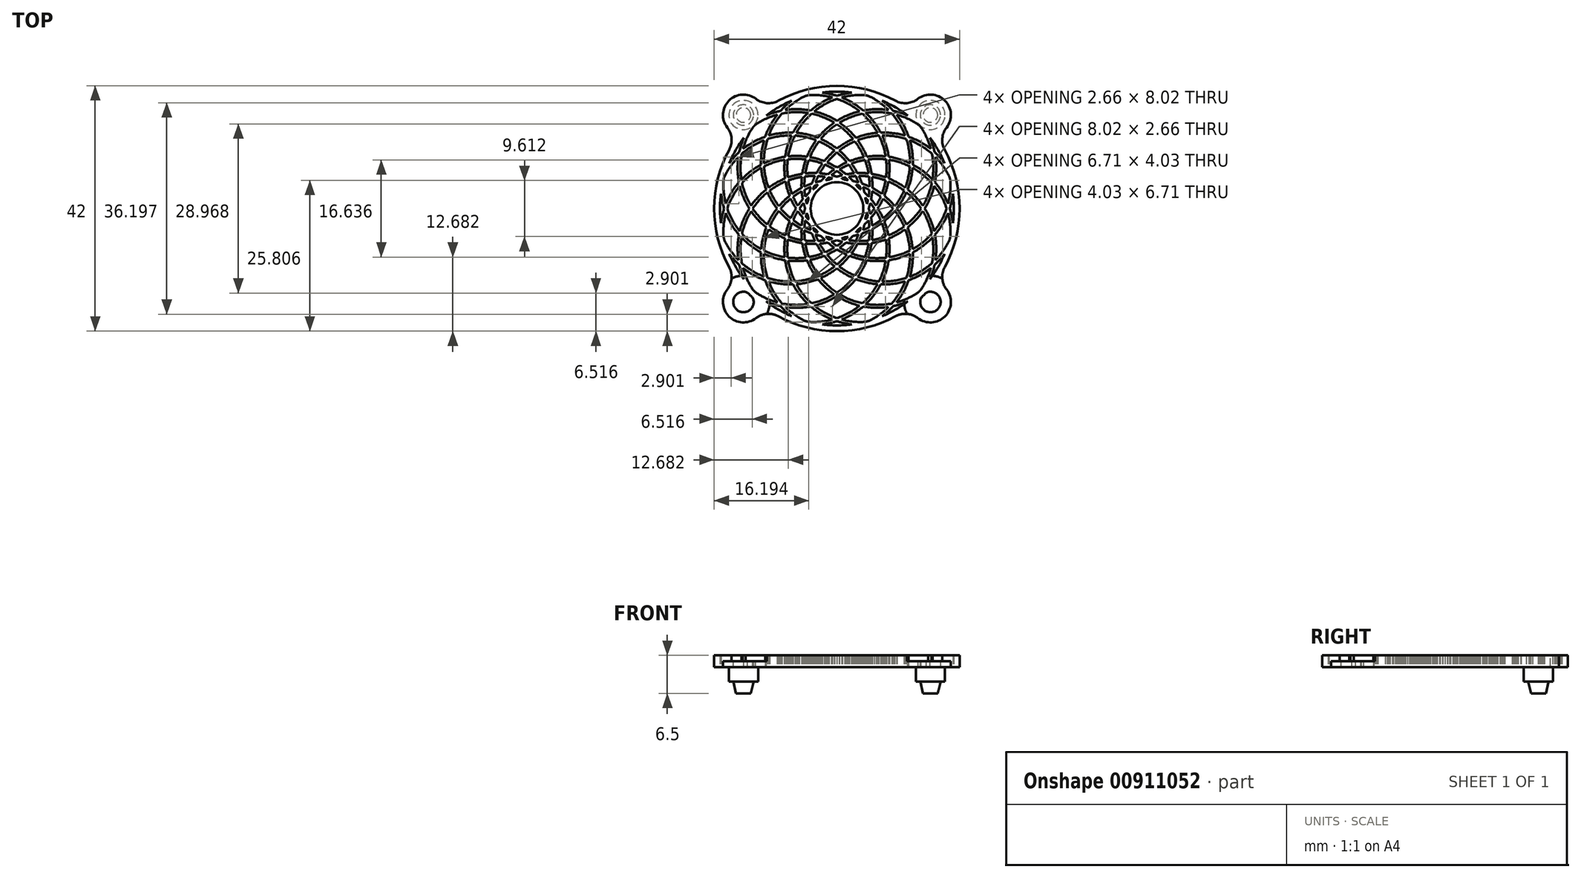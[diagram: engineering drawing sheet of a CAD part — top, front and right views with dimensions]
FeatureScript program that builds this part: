
annotation { "Feature Type Name" : "Feature", "Feature Type Description" : "" }
export const myFeature = defineFeature(function(context is Context, id is Id, definition is map)
    precondition{}
    {
        {
            var Q0;
            Q0=qCreatedBy(makeId("Top.planeOp"),FACE);
            var sketch = newSketch(context, id + "F0", { "sketchPlane" : qUnion([Q0])});
            skArc(sketch, "E0", {"start": v(-16.8, 12.6) * mm, "mid": v(-21, 0) * mm, "end": v(-16.8, -12.6) * mm});
            skArc(sketch, "E1", {"start": v(-7.75, 18.44) * mm, "mid": v(-8.74, 17.62) * mm, "end": v(-9.65, 16.71) * mm});
            skArc(sketch, "E2.1.0", {"start": v(-15.93, 12.1) * mm, "mid": v(-16.38, 10.89) * mm, "end": v(-16.71, 9.65) * mm});
            skArc(sketch, "E2.2.0", {"start": v(-19.84, 2.5) * mm, "mid": v(-19.63, 1.24) * mm, "end": v(-19.3, 0) * mm});
            skArc(sketch, "E2.3.0", {"start": v(-18.44, -7.75) * mm, "mid": v(-17.62, -8.74) * mm, "end": v(-16.71, -9.65) * mm});
            skArc(sketch, "E2.4.0", {"start": v(-19.3, 0) * mm, "mid": v(-19.63, -1.24) * mm, "end": v(-19.84, -2.5) * mm});
            skArc(sketch, "E2.5.0", {"start": v(-2.5, -19.84) * mm, "mid": v(-1.24, -19.63) * mm, "end": v(0, -19.3) * mm});
            skArc(sketch, "E2.6.0", {"start": v(7.75, -18.44) * mm, "mid": v(8.74, -17.62) * mm, "end": v(9.65, -16.71) * mm});
            skArc(sketch, "E2.7.0", {"start": v(15.93, -12.1) * mm, "mid": v(16.38, -10.89) * mm, "end": v(16.71, -9.65) * mm});
            skArc(sketch, "E2.8.0", {"start": v(19.84, -2.5) * mm, "mid": v(19.63, -1.24) * mm, "end": v(19.3, 0) * mm});
            skArc(sketch, "E2.9.0", {"start": v(18.44, 7.75) * mm, "mid": v(17.62, 8.74) * mm, "end": v(16.71, 9.65) * mm});
            skArc(sketch, "E2.10.0", {"start": v(12.1, 15.93) * mm, "mid": v(10.89, 16.38) * mm, "end": v(9.65, 16.71) * mm});
            skArc(sketch, "E2.11.0", {"start": v(2.5, 19.84) * mm, "mid": v(1.24, 19.63) * mm, "end": v(0, 19.3) * mm});
            skArc(sketch, "E3", {"start": v(16.8, 12.6) * mm, "mid": v(18.47, 18.47) * mm, "end": v(12.6, 16.8) * mm});
            skArc(sketch, "E4.3.0", {"start": v(12.6, -16.8) * mm, "mid": v(18.47, -18.47) * mm, "end": v(16.8, -12.6) * mm});
            skArc(sketch, "E5.2.0", {"start": v(-15.28, -14.4) * mm, "mid": v(-17.24, -17.24) * mm, "end": v(-14.4, -15.28) * mm});
            skArc(sketch, "E6.1.3.0", {"start": v(14.4, -15.28) * mm, "mid": v(17.24, -17.24) * mm, "end": v(15.28, -14.4) * mm});
            skPoint(sketch, "E7.orphan", {"position": v(-16, 16) * mm});
            skArc(sketch, "E8.trimOffspring", {"start": v(-12.6, 16.8) * mm, "mid": v(-18.47, 18.47) * mm, "end": v(-16.8, 12.6) * mm});
            skArc(sketch, "E9.trimOffspring", {"start": v(-16.8, -12.6) * mm, "mid": v(-18.47, -18.47) * mm, "end": v(-12.6, -16.8) * mm});
            skArc(sketch, "E10", {"start": v(14.36, 13.92) * mm, "mid": v(14.14, 14.14) * mm, "end": v(13.92, 14.36) * mm});
            skArc(sketch, "E11", {"start": v(-5.48, 19.23) * mm, "mid": v(-7.25, 18.19) * mm, "end": v(-8.82, 16.86) * mm});
            skArc(sketch, "E12.1.0", {"start": v(-14.36, 13.92) * mm, "mid": v(-15.37, 12.13) * mm, "end": v(-16.07, 10.2) * mm});
            skArc(sketch, "E12.2.0", {"start": v(-19.37, 5.2) * mm, "mid": v(-19.39, 2.98) * mm, "end": v(-19.01, 0.8) * mm});
            skArc(sketch, "E12.3.0", {"start": v(-16.86, 8.82) * mm, "mid": v(-18.28, 7.11) * mm, "end": v(-19.37, 5.2) * mm});
            skArc(sketch, "E12.4.0", {"start": v(-19.01, -0.8) * mm, "mid": v(-19.37, -2.82) * mm, "end": v(-19.4, -4.87) * mm});
            skArc(sketch, "E12.5.0", {"start": v(-4.87, -19.4) * mm, "mid": v(-2.82, -19.37) * mm, "end": v(-0.8, -19.01) * mm});
            skArc(sketch, "E12.6.0", {"start": v(5.48, -19.23) * mm, "mid": v(7.25, -18.19) * mm, "end": v(8.82, -16.86) * mm});
            skArc(sketch, "E12.7.0", {"start": v(14.36, -13.92) * mm, "mid": v(15.37, -12.13) * mm, "end": v(16.07, -10.2) * mm});
            skArc(sketch, "E12.8.0", {"start": v(19.4, -4.87) * mm, "mid": v(19.37, -2.82) * mm, "end": v(19.01, -0.8) * mm});
            skArc(sketch, "E12.9.0", {"start": v(19.23, 5.48) * mm, "mid": v(18.19, 7.25) * mm, "end": v(16.86, 8.82) * mm});
            skArc(sketch, "E12.10.0", {"start": v(13.92, 14.36) * mm, "mid": v(12.13, 15.37) * mm, "end": v(10.2, 16.07) * mm});
            skArc(sketch, "E12.11.0", {"start": v(4.87, 19.4) * mm, "mid": v(2.82, 19.37) * mm, "end": v(0.8, 19.01) * mm});
            skCircle(sketch, "E13", {"center": v(0, 0) * mm, "radius": 4.5 * mm});
            skArc(sketch, "E14.trimOffspring", {"start": v(12.6, 16.8) * mm, "mid": v(0, 21) * mm, "end": v(-12.6, 16.8) * mm});
            skArc(sketch, "E15.trimOffspring", {"start": v(12.1, 15.93) * mm, "mid": v(10, 17.32) * mm, "end": v(7.75, 18.44) * mm});
            skArc(sketch, "E16.trimOffspring", {"start": v(-7.75, 18.44) * mm, "mid": v(-10, 17.32) * mm, "end": v(-12.1, 15.93) * mm});
            skArc(sketch, "E17.trimOffspring", {"start": v(-4.87, 19.4) * mm, "mid": v(-5.18, 19.32) * mm, "end": v(-5.48, 19.23) * mm});
            skArc(sketch, "E18.trimOffspring", {"start": v(-13.92, 14.36) * mm, "mid": v(-14.14, 14.14) * mm, "end": v(-14.36, 13.92) * mm});
            skArc(sketch, "E19.trimOffspring", {"start": v(-15.93, 12.1) * mm, "mid": v(-17.32, 10) * mm, "end": v(-18.44, 7.75) * mm});
            skArc(sketch, "E20.trimOffspring", {"start": v(-16.86, 8.82) * mm, "mid": v(-17, 6.65) * mm, "end": v(-16.77, 4.5) * mm});
            skArc(sketch, "E21.trimOffspring", {"start": v(-16.71, 9.65) * mm, "mid": v(-17.62, 8.74) * mm, "end": v(-18.44, 7.75) * mm});
            skArc(sketch, "E22.trimOffspring", {"start": v(-16.26, 9.39) * mm, "mid": v(-16.31, 4.78) * mm, "end": v(-14.7, 0.46) * mm});
            skArc(sketch, "E23.trimOffspring", {"start": v(-19.23, -5.48) * mm, "mid": v(-18.19, -7.25) * mm, "end": v(-16.86, -8.82) * mm});
            skArc(sketch, "E24.trimOffspring", {"start": v(-19.84, 2.5) * mm, "mid": v(-20, 0) * mm, "end": v(-19.84, -2.5) * mm});
            skArc(sketch, "E25.trimOffspring", {"start": v(-18.77, 0) * mm, "mid": v(-17.88, -2.03) * mm, "end": v(-16.64, -3.87) * mm});
            skArc(sketch, "E26.trimOffspring", {"start": v(-19.01, -0.8) * mm, "mid": v(-18.05, -2.74) * mm, "end": v(-16.77, -4.5) * mm});
            skArc(sketch, "E27.trimOffspring", {"start": v(-19.4, -4.87) * mm, "mid": v(-19.32, -5.18) * mm, "end": v(-19.23, -5.48) * mm});
            skArc(sketch, "E28.trimOffspring", {"start": v(-18.44, -7.75) * mm, "mid": v(-17.32, -10) * mm, "end": v(-15.93, -12.1) * mm});
            skArc(sketch, "E29.trimOffspring", {"start": v(-13.92, -14.36) * mm, "mid": v(-12.13, -15.37) * mm, "end": v(-10.2, -16.07) * mm});
            skArc(sketch, "E30.trimOffspring", {"start": v(19.4, 4.87) * mm, "mid": v(19.32, 5.18) * mm, "end": v(19.23, 5.48) * mm});
            skArc(sketch, "E31.trimOffspring", {"start": v(18.44, 7.75) * mm, "mid": v(17.32, 10) * mm, "end": v(15.93, 12.1) * mm});
            skArc(sketch, "E32.trimOffspring", {"start": v(5.48, 19.23) * mm, "mid": v(5.18, 19.32) * mm, "end": v(4.87, 19.4) * mm});
            skArc(sketch, "E33.trimOffspring", {"start": v(2.5, 19.84) * mm, "mid": v(0, 20) * mm, "end": v(-2.5, 19.84) * mm});
            skArc(sketch, "E34.trimOffspring", {"start": v(15.93, -12.1) * mm, "mid": v(17.32, -10) * mm, "end": v(18.44, -7.75) * mm});
            skArc(sketch, "E35.trimOffspring", {"start": v(19.23, -5.48) * mm, "mid": v(19.32, -5.18) * mm, "end": v(19.4, -4.87) * mm});
            skArc(sketch, "E36.trimOffspring", {"start": v(14.4, -15.28) * mm, "mid": v(14.85, -14.85) * mm, "end": v(15.28, -14.4) * mm});
            skArc(sketch, "E37.trimOffspring", {"start": v(13.92, -14.36) * mm, "mid": v(14.14, -14.14) * mm, "end": v(14.36, -13.92) * mm});
            skArc(sketch, "E38.trimOffspring", {"start": v(16.8, -12.6) * mm, "mid": v(21, 0) * mm, "end": v(16.8, 12.6) * mm});
            skArc(sketch, "E39.trimOffspring", {"start": v(7.75, -18.44) * mm, "mid": v(10, -17.32) * mm, "end": v(12.1, -15.93) * mm});
            skArc(sketch, "E40.trimOffspring", {"start": v(4.87, -19.4) * mm, "mid": v(5.18, -19.32) * mm, "end": v(5.48, -19.23) * mm});
            skArc(sketch, "E41.trimOffspring", {"start": v(-5.48, -19.23) * mm, "mid": v(-5.18, -19.32) * mm, "end": v(-4.87, -19.4) * mm});
            skArc(sketch, "E42.trimOffspring", {"start": v(-2.5, -19.84) * mm, "mid": v(0, -20) * mm, "end": v(2.5, -19.84) * mm});
            skArc(sketch, "E43.trimOffspring", {"start": v(-12.6, -16.8) * mm, "mid": v(0, -21) * mm, "end": v(12.6, -16.8) * mm});
            skArc(sketch, "E44.trimOffspring", {"start": v(-15.28, -14.4) * mm, "mid": v(-14.85, -14.85) * mm, "end": v(-14.4, -15.28) * mm});
            skArc(sketch, "E45.trimOffspring", {"start": v(-12.1, -15.93) * mm, "mid": v(-10.89, -16.38) * mm, "end": v(-9.65, -16.71) * mm});
            skArc(sketch, "E46.trimOffspring", {"start": v(-12.1, -15.93) * mm, "mid": v(-10, -17.32) * mm, "end": v(-7.75, -18.44) * mm});
            skArc(sketch, "E47.trimOffspring", {"start": v(-14.36, -13.92) * mm, "mid": v(-14.14, -14.14) * mm, "end": v(-13.92, -14.36) * mm});
            skArc(sketch, "E48.trimOffspring", {"start": v(-12.47, 11.67) * mm, "mid": v(-12.9, 9.6) * mm, "end": v(-13, 7.5) * mm});
            skArc(sketch, "E49.trimOffspring", {"start": v(-11.88, 11.88) * mm, "mid": v(-12.36, 9.84) * mm, "end": v(-12.5, 7.75) * mm});
            skArc(sketch, "E50.trimOffspring", {"start": v(-12.47, 11.67) * mm, "mid": v(-14.47, 10.7) * mm, "end": v(-16.26, 9.39) * mm});
            skArc(sketch, "E51.trimOffspring", {"start": v(-12.28, 12.28) * mm, "mid": v(-14.26, 11.4) * mm, "end": v(-16.07, 10.2) * mm});
            skArc(sketch, "E52.trimOffspring", {"start": v(-7.5, 13) * mm, "mid": v(-9.6, 12.9) * mm, "end": v(-11.67, 12.47) * mm});
            skArc(sketch, "E53.trimOffspring", {"start": v(-7.75, 12.5) * mm, "mid": v(-8.44, 10.72) * mm, "end": v(-8.86, 8.86) * mm});
            skArc(sketch, "E54.trimOffspring", {"start": v(-7.2, 12.47) * mm, "mid": v(-7.9, 10.74) * mm, "end": v(-8.34, 8.92) * mm});
            skArc(sketch, "E55.trimOffspring", {"start": v(-7.75, 12.5) * mm, "mid": v(-9.84, 12.36) * mm, "end": v(-11.88, 11.88) * mm});
            skArc(sketch, "E56.trimOffspring", {"start": v(-3.56, 11.68) * mm, "mid": v(-5.35, 12.22) * mm, "end": v(-7.2, 12.47) * mm});
            skArc(sketch, "E57.trimOffspring", {"start": v(-3.24, 12.1) * mm, "mid": v(-5.06, 12.66) * mm, "end": v(-6.95, 12.96) * mm});
            skArc(sketch, "E58.trimOffspring", {"start": v(-3.56, 11.68) * mm, "mid": v(-4.43, 10.33) * mm, "end": v(-5.12, 8.87) * mm});
            skArc(sketch, "E59.trimOffspring", {"start": v(-5.12, 8.87) * mm, "mid": v(-6.73, 9) * mm, "end": v(-8.34, 8.92) * mm});
            skArc(sketch, "E60.trimOffspring", {"start": v(-5.3, 8.4) * mm, "mid": v(-5.68, 7.18) * mm, "end": v(-5.93, 5.93) * mm});
            skArc(sketch, "E61.trimOffspring", {"start": v(-3.08, 11.5) * mm, "mid": v(-3.93, 10.19) * mm, "end": v(-4.62, 8.8) * mm});
            skArc(sketch, "E62.trimOffspring", {"start": v(-5.3, 8.4) * mm, "mid": v(-6.86, 8.5) * mm, "end": v(-8.41, 8.41) * mm});
            skArc(sketch, "E63.trimOffspring", {"start": v(-2.49, 7.68) * mm, "mid": v(-3.02, 6.9) * mm, "end": v(-3.5, 6.06) * mm});
            skArc(sketch, "E64.trimOffspring", {"start": v(-2.17, 8.1) * mm, "mid": v(-3.38, 8.5) * mm, "end": v(-4.62, 8.8) * mm});
            skArc(sketch, "E65.trimOffspring", {"start": v(-2.49, 7.68) * mm, "mid": v(-3.63, 8.06) * mm, "end": v(-4.8, 8.32) * mm});
            skArc(sketch, "E66.trimOffspring", {"start": v(-2, 7.5) * mm, "mid": v(-2.5, 6.78) * mm, "end": v(-2.95, 6.03) * mm});
            skArc(sketch, "E67.trimOffspring", {"start": v(-0.4, 9.92) * mm, "mid": v(-1.69, 10.8) * mm, "end": v(-3.08, 11.5) * mm});
            skArc(sketch, "E68.trimOffspring", {"start": v(-0.4, 9.92) * mm, "mid": v(-1.33, 9.05) * mm, "end": v(-2.17, 8.1) * mm});
            skArc(sketch, "E69.trimOffspring", {"start": v(0, 10.25) * mm, "mid": v(-1.33, 11.16) * mm, "end": v(-2.76, 11.9) * mm});
            skArc(sketch, "E70.trimOffspring", {"start": v(0, 9.6) * mm, "mid": v(-0.89, 8.8) * mm, "end": v(-1.69, 7.9) * mm});
            skArc(sketch, "E71.trimOffspring", {"start": v(0, 15) * mm, "mid": v(-1.87, 15.98) * mm, "end": v(-3.87, 16.64) * mm});
            skArc(sketch, "E72.trimOffspring", {"start": v(-0.46, 14.7) * mm, "mid": v(-1.95, 13.5) * mm, "end": v(-3.24, 12.1) * mm});
            skArc(sketch, "E73.trimOffspring", {"start": v(0, 14.4) * mm, "mid": v(-1.47, 13.25) * mm, "end": v(-2.76, 11.9) * mm});
            skArc(sketch, "E74.trimOffspring", {"start": v(-0.46, 14.7) * mm, "mid": v(-2.34, 15.63) * mm, "end": v(-4.35, 16.23) * mm});
            skArc(sketch, "E75.trimOffspring", {"start": v(6.95, 12.96) * mm, "mid": v(5.06, 12.66) * mm, "end": v(3.24, 12.1) * mm});
            skArc(sketch, "E76.trimOffspring", {"start": v(7.5, 13) * mm, "mid": v(6.37, 14.77) * mm, "end": v(4.96, 16.34) * mm});
            skArc(sketch, "E77.trimOffspring", {"start": v(6.95, 12.96) * mm, "mid": v(5.79, 14.7) * mm, "end": v(4.35, 16.23) * mm});
            skArc(sketch, "E78.trimOffspring", {"start": v(7.2, 12.47) * mm, "mid": v(5.35, 12.22) * mm, "end": v(3.56, 11.68) * mm});
            skArc(sketch, "E79.trimOffspring", {"start": v(3.24, 12.1) * mm, "mid": v(1.95, 13.5) * mm, "end": v(0.46, 14.7) * mm});
            skArc(sketch, "E80.trimOffspring", {"start": v(2.76, 11.9) * mm, "mid": v(1.47, 13.25) * mm, "end": v(0, 14.4) * mm});
            skArc(sketch, "E81.trimOffspring", {"start": v(2.76, 11.9) * mm, "mid": v(1.33, 11.16) * mm, "end": v(0, 10.25) * mm});
            skArc(sketch, "E82.trimOffspring", {"start": v(3.08, 11.5) * mm, "mid": v(1.69, 10.8) * mm, "end": v(0.4, 9.92) * mm});
            skArc(sketch, "E83.trimOffspring", {"start": v(9.65, 16.71) * mm, "mid": v(8.74, 17.62) * mm, "end": v(7.75, 18.44) * mm});
            skArc(sketch, "E84.trimOffspring", {"start": v(8.82, 16.86) * mm, "mid": v(7.25, 18.19) * mm, "end": v(5.48, 19.23) * mm});
            skArc(sketch, "E85.trimOffspring", {"start": v(9.39, 16.26) * mm, "mid": v(7.18, 16.5) * mm, "end": v(4.96, 16.34) * mm});
            skArc(sketch, "E86.trimOffspring", {"start": v(8.82, 16.86) * mm, "mid": v(6.65, 17) * mm, "end": v(4.5, 16.77) * mm});
            skArc(sketch, "E87.trimOffspring", {"start": v(3.87, 16.64) * mm, "mid": v(2.03, 17.88) * mm, "end": v(0, 18.77) * mm});
            skArc(sketch, "E88.trimOffspring", {"start": v(3.87, 16.64) * mm, "mid": v(1.87, 15.98) * mm, "end": v(0, 15) * mm});
            skArc(sketch, "E89.trimOffspring", {"start": v(4.5, 16.77) * mm, "mid": v(2.74, 18.05) * mm, "end": v(0.8, 19.01) * mm});
            skArc(sketch, "E90.trimOffspring", {"start": v(4.35, 16.23) * mm, "mid": v(2.34, 15.63) * mm, "end": v(0.46, 14.7) * mm});
            skArc(sketch, "E91.trimOffspring", {"start": v(0, 18.77) * mm, "mid": v(-2.03, 17.88) * mm, "end": v(-3.87, 16.64) * mm});
            skArc(sketch, "E92.trimOffspring", {"start": v(0, 19.3) * mm, "mid": v(-1.24, 19.63) * mm, "end": v(-2.5, 19.84) * mm});
            skArc(sketch, "E93.trimOffspring", {"start": v(-0.8, 19.01) * mm, "mid": v(-2.82, 19.37) * mm, "end": v(-4.87, 19.4) * mm});
            skArc(sketch, "E94.trimOffspring", {"start": v(-0.8, 19.01) * mm, "mid": v(-2.74, 18.05) * mm, "end": v(-4.5, 16.77) * mm});
            skArc(sketch, "E95.trimOffspring", {"start": v(-4.5, 16.77) * mm, "mid": v(-6.65, 17) * mm, "end": v(-8.82, 16.86) * mm});
            skArc(sketch, "E96.trimOffspring", {"start": v(-4.96, 16.34) * mm, "mid": v(-6.37, 14.77) * mm, "end": v(-7.5, 13) * mm});
            skArc(sketch, "E97.trimOffspring", {"start": v(-4.96, 16.34) * mm, "mid": v(-7.18, 16.5) * mm, "end": v(-9.39, 16.26) * mm});
            skArc(sketch, "E98.trimOffspring", {"start": v(-4.35, 16.23) * mm, "mid": v(-5.79, 14.7) * mm, "end": v(-6.95, 12.96) * mm});
            skArc(sketch, "E99.trimOffspring", {"start": v(-9.65, 16.71) * mm, "mid": v(-10.89, 16.38) * mm, "end": v(-12.1, 15.93) * mm});
            skArc(sketch, "E100.trimOffspring", {"start": v(-10.2, 16.07) * mm, "mid": v(-11.4, 14.26) * mm, "end": v(-12.28, 12.28) * mm});
            skArc(sketch, "E101.trimOffspring", {"start": v(-10.2, 16.07) * mm, "mid": v(-12.13, 15.37) * mm, "end": v(-13.92, 14.36) * mm});
            skArc(sketch, "E102.trimOffspring", {"start": v(-9.39, 16.26) * mm, "mid": v(-10.7, 14.47) * mm, "end": v(-11.67, 12.47) * mm});
            skArc(sketch, "E103.trimOffspring", {"start": v(-8.41, 8.41) * mm, "mid": v(-8.5, 6.86) * mm, "end": v(-8.4, 5.3) * mm});
            skArc(sketch, "E104.trimOffspring", {"start": v(-8.86, 8.86) * mm, "mid": v(-10.72, 8.44) * mm, "end": v(-12.5, 7.75) * mm});
            skArc(sketch, "E105.trimOffspring", {"start": v(-12.47, 7.2) * mm, "mid": v(-12.22, 5.35) * mm, "end": v(-11.68, 3.56) * mm});
            skArc(sketch, "E106.trimOffspring", {"start": v(-4.71, -2.72) * mm, "mid": v(-4.6, -3.2) * mm, "end": v(-4.47, -3.67) * mm});
            skArc(sketch, "E107.trimOffspring", {"start": v(-5.42, -2.03) * mm, "mid": v(-5.5, -2.62) * mm, "end": v(-5.55, -3.2) * mm});
            skArc(sketch, "E108.trimOffspring", {"start": v(-5.57, -3.75) * mm, "mid": v(-5.56, -4.62) * mm, "end": v(-5.48, -5.48) * mm});
            skArc(sketch, "E109.trimOffspring", {"start": v(-6.06, -3.5) * mm, "mid": v(-6.06, -4.46) * mm, "end": v(-6, -5.41) * mm});
            skArc(sketch, "E110.trimOffspring", {"start": v(-5.84, -1.57) * mm, "mid": v(-5.95, -2.26) * mm, "end": v(-6.03, -2.95) * mm});
            skArc(sketch, "E111.trimOffspring", {"start": v(-5.3, -1.42) * mm, "mid": v(-5.09, -1.66) * mm, "end": v(-4.86, -1.89) * mm});
            skArc(sketch, "E112.trimOffspring", {"start": v(-5.42, -2.03) * mm, "mid": v(-5.07, -2.38) * mm, "end": v(-4.71, -2.72) * mm});
            skArc(sketch, "E113.trimOffspring", {"start": v(-5.57, -3.75) * mm, "mid": v(-4.93, -4.03) * mm, "end": v(-4.28, -4.28) * mm});
            skArc(sketch, "E114.trimOffspring", {"start": v(-5.55, -3.2) * mm, "mid": v(-5.01, -3.45) * mm, "end": v(-4.47, -3.67) * mm});
            skArc(sketch, "E115.trimOffspring", {"start": v(-5.15, -0.8) * mm, "mid": v(-5.05, -1.06) * mm, "end": v(-4.93, -1.32) * mm});
            skArc(sketch, "E116.trimOffspring", {"start": v(-5.7, 0.95) * mm, "mid": v(-6.07, 0.48) * mm, "end": v(-6.4, 0) * mm});
            skArc(sketch, "E117.trimOffspring", {"start": v(-5.3, 1.42) * mm, "mid": v(-5.23, 1.1) * mm, "end": v(-5.15, 0.8) * mm});
            skArc(sketch, "E118.trimOffspring", {"start": v(-5.84, 1.57) * mm, "mid": v(-6.28, 1.02) * mm, "end": v(-6.7, 0.46) * mm});
            skArc(sketch, "E119.trimOffspring", {"start": v(-5.7, 0.95) * mm, "mid": v(-5.58, 0.47) * mm, "end": v(-5.44, 0) * mm});
            skArc(sketch, "E120.trimOffspring", {"start": v(-5.44, 0) * mm, "mid": v(-5.58, -0.47) * mm, "end": v(-5.7, -0.95) * mm});
            skArc(sketch, "E121.trimOffspring", {"start": v(-4.93, -1.32) * mm, "mid": v(-4.9, -1.6) * mm, "end": v(-4.86, -1.89) * mm});
            skArc(sketch, "E122.trimOffspring", {"start": v(-4.86, 1.89) * mm, "mid": v(-5.09, 1.66) * mm, "end": v(-5.3, 1.42) * mm});
            skArc(sketch, "E123.trimOffspring", {"start": v(-4.86, 1.89) * mm, "mid": v(-4.9, 1.6) * mm, "end": v(-4.93, 1.32) * mm});
            skArc(sketch, "E124.trimOffspring", {"start": v(-4.71, 2.72) * mm, "mid": v(-5.07, 2.38) * mm, "end": v(-5.42, 2.03) * mm});
            skArc(sketch, "E125.trimOffspring", {"start": v(-4.47, 3.67) * mm, "mid": v(-5.01, 3.45) * mm, "end": v(-5.55, 3.2) * mm});
            skArc(sketch, "E126.trimOffspring", {"start": v(-4.28, 4.28) * mm, "mid": v(-4.93, 4.03) * mm, "end": v(-5.57, 3.75) * mm});
            skArc(sketch, "E127.trimOffspring", {"start": v(-4.47, 3.67) * mm, "mid": v(-4.6, 3.2) * mm, "end": v(-4.71, 2.72) * mm});
            skArc(sketch, "E128.trimOffspring", {"start": v(-3.27, 4.07) * mm, "mid": v(-3.44, 3.84) * mm, "end": v(-3.61, 3.61) * mm});
            skArc(sketch, "E129.trimOffspring", {"start": v(-3.27, 4.07) * mm, "mid": v(-3.58, 3.98) * mm, "end": v(-3.88, 3.88) * mm});
            skArc(sketch, "E130.trimOffspring", {"start": v(-4.93, 1.32) * mm, "mid": v(-5.05, 1.06) * mm, "end": v(-5.15, 0.8) * mm});
            skArc(sketch, "E131.trimOffspring", {"start": v(-4.07, -3.27) * mm, "mid": v(-3.84, -3.44) * mm, "end": v(-3.61, -3.61) * mm});
            skArc(sketch, "E132.trimOffspring", {"start": v(-5.15, -0.8) * mm, "mid": v(-5.23, -1.1) * mm, "end": v(-5.3, -1.42) * mm});
            skArc(sketch, "E133.trimOffspring", {"start": v(-6.4, 0) * mm, "mid": v(-6.07, -0.48) * mm, "end": v(-5.7, -0.95) * mm});
            skArc(sketch, "E134.trimOffspring", {"start": v(-6.7, -0.46) * mm, "mid": v(-7.12, -1.22) * mm, "end": v(-7.5, -2) * mm});
            skArc(sketch, "E135.trimOffspring", {"start": v(-7.5, -2) * mm, "mid": v(-6.78, -2.5) * mm, "end": v(-6.03, -2.95) * mm});
            skArc(sketch, "E136.trimOffspring", {"start": v(-7, 0) * mm, "mid": v(-7.48, -0.83) * mm, "end": v(-7.9, -1.69) * mm});
            skArc(sketch, "E137.trimOffspring", {"start": v(-7.68, -2.49) * mm, "mid": v(-6.9, -3.02) * mm, "end": v(-6.06, -3.5) * mm});
            skArc(sketch, "E138.trimOffspring", {"start": v(-7.68, -2.49) * mm, "mid": v(-8.06, -3.63) * mm, "end": v(-8.32, -4.8) * mm});
            skArc(sketch, "E139.trimOffspring", {"start": v(-8.1, -2.17) * mm, "mid": v(-8.5, -3.38) * mm, "end": v(-8.8, -4.62) * mm});
            skArc(sketch, "E140.trimOffspring", {"start": v(-3.88, -3.88) * mm, "mid": v(-3.58, -3.98) * mm, "end": v(-3.27, -4.07) * mm});
            skArc(sketch, "E141.trimOffspring", {"start": v(-3.67, -4.47) * mm, "mid": v(-3.2, -4.6) * mm, "end": v(-2.72, -4.71) * mm});
            skArc(sketch, "E142.trimOffspring", {"start": v(-4.28, -4.28) * mm, "mid": v(-4.03, -4.93) * mm, "end": v(-3.75, -5.57) * mm});
            skArc(sketch, "E143.trimOffspring", {"start": v(-3.67, -4.47) * mm, "mid": v(-3.45, -5.01) * mm, "end": v(-3.2, -5.55) * mm});
            skArc(sketch, "E144.trimOffspring", {"start": v(-2.72, -4.71) * mm, "mid": v(-2.38, -5.07) * mm, "end": v(-2.03, -5.42) * mm});
            skArc(sketch, "E145.trimOffspring", {"start": v(-1.89, -4.86) * mm, "mid": v(-1.6, -4.9) * mm, "end": v(-1.32, -4.93) * mm});
            skArc(sketch, "E146.trimOffspring", {"start": v(-4.07, -3.27) * mm, "mid": v(-3.98, -3.58) * mm, "end": v(-3.88, -3.88) * mm});
            skArc(sketch, "E147.trimOffspring", {"start": v(-3.61, -3.61) * mm, "mid": v(-3.44, -3.84) * mm, "end": v(-3.27, -4.07) * mm});
            skArc(sketch, "E148.trimOffspring", {"start": v(-3.5, -6.06) * mm, "mid": v(-3.02, -6.9) * mm, "end": v(-2.49, -7.68) * mm});
            skArc(sketch, "E149.trimOffspring", {"start": v(-3.2, -5.55) * mm, "mid": v(-2.62, -5.5) * mm, "end": v(-2.03, -5.42) * mm});
            skArc(sketch, "E150.trimOffspring", {"start": v(-2.95, -6.03) * mm, "mid": v(-2.5, -6.78) * mm, "end": v(-2, -7.5) * mm});
            skArc(sketch, "E151.trimOffspring", {"start": v(-1.57, -5.84) * mm, "mid": v(-1.02, -6.28) * mm, "end": v(-0.46, -6.7) * mm});
            skArc(sketch, "E152.trimOffspring", {"start": v(-0.95, -5.7) * mm, "mid": v(-0.48, -6.07) * mm, "end": v(0, -6.4) * mm});
            skArc(sketch, "E153.trimOffspring", {"start": v(-0.95, -5.7) * mm, "mid": v(-0.47, -5.58) * mm, "end": v(0, -5.44) * mm});
            skArc(sketch, "E154.trimOffspring", {"start": v(-1.42, -5.3) * mm, "mid": v(-1.1, -5.23) * mm, "end": v(-0.8, -5.15) * mm});
            skArc(sketch, "E155.trimOffspring", {"start": v(0, -5.44) * mm, "mid": v(0.47, -5.58) * mm, "end": v(0.95, -5.7) * mm});
            skArc(sketch, "E156.trimOffspring", {"start": v(-1.89, -4.86) * mm, "mid": v(-1.66, -5.09) * mm, "end": v(-1.42, -5.3) * mm});
            skArc(sketch, "E157.trimOffspring", {"start": v(-1.32, -4.93) * mm, "mid": v(-1.06, -5.05) * mm, "end": v(-0.8, -5.15) * mm});
            skArc(sketch, "E158.trimOffspring", {"start": v(0.8, -5.15) * mm, "mid": v(1.06, -5.05) * mm, "end": v(1.32, -4.93) * mm});
            skArc(sketch, "E159.trimOffspring", {"start": v(2.03, -5.42) * mm, "mid": v(2.38, -5.07) * mm, "end": v(2.72, -4.71) * mm});
            skArc(sketch, "E160.trimOffspring", {"start": v(1.42, -5.3) * mm, "mid": v(1.66, -5.09) * mm, "end": v(1.89, -4.86) * mm});
            skArc(sketch, "E161.trimOffspring", {"start": v(0.46, -6.7) * mm, "mid": v(1.02, -6.28) * mm, "end": v(1.57, -5.84) * mm});
            skArc(sketch, "E162.trimOffspring", {"start": v(0, -6.4) * mm, "mid": v(0.48, -6.07) * mm, "end": v(0.95, -5.7) * mm});
            skArc(sketch, "E163.trimOffspring", {"start": v(0, -7) * mm, "mid": v(0.83, -7.48) * mm, "end": v(1.69, -7.9) * mm});
            skArc(sketch, "E164.trimOffspring", {"start": v(0.46, -6.7) * mm, "mid": v(1.22, -7.12) * mm, "end": v(2, -7.5) * mm});
            skArc(sketch, "E165.trimOffspring", {"start": v(1.57, -5.84) * mm, "mid": v(2.26, -5.95) * mm, "end": v(2.95, -6.03) * mm});
            skArc(sketch, "E166.trimOffspring", {"start": v(2.03, -5.42) * mm, "mid": v(2.62, -5.5) * mm, "end": v(3.2, -5.55) * mm});
            skArc(sketch, "E167.trimOffspring", {"start": v(2.72, -4.71) * mm, "mid": v(3.2, -4.6) * mm, "end": v(3.67, -4.47) * mm});
            skArc(sketch, "E168.trimOffspring", {"start": v(0.8, -5.15) * mm, "mid": v(1.1, -5.23) * mm, "end": v(1.42, -5.3) * mm});
            skArc(sketch, "E169.trimOffspring", {"start": v(1.32, -4.93) * mm, "mid": v(1.6, -4.9) * mm, "end": v(1.89, -4.86) * mm});
            skArc(sketch, "E170.trimOffspring", {"start": v(-3.61, 3.61) * mm, "mid": v(-3.84, 3.44) * mm, "end": v(-4.07, 3.27) * mm});
            skArc(sketch, "E171.trimOffspring", {"start": v(-2.72, 4.71) * mm, "mid": v(-3.2, 4.6) * mm, "end": v(-3.67, 4.47) * mm});
            skArc(sketch, "E172.trimOffspring", {"start": v(0, 5.44) * mm, "mid": v(-0.47, 5.58) * mm, "end": v(-0.95, 5.7) * mm});
            skArc(sketch, "E173.trimOffspring", {"start": v(-3.75, 5.57) * mm, "mid": v(-4.62, 5.56) * mm, "end": v(-5.48, 5.48) * mm});
            skArc(sketch, "E174.trimOffspring", {"start": v(-3.75, 5.57) * mm, "mid": v(-4.03, 4.93) * mm, "end": v(-4.28, 4.28) * mm});
            skArc(sketch, "E175.trimOffspring", {"start": v(-3.5, 6.06) * mm, "mid": v(-4.46, 6.06) * mm, "end": v(-5.41, 6) * mm});
            skArc(sketch, "E176.trimOffspring", {"start": v(-3.2, 5.55) * mm, "mid": v(-3.45, 5.01) * mm, "end": v(-3.67, 4.47) * mm});
            skArc(sketch, "E177.trimOffspring", {"start": v(-2.03, 5.42) * mm, "mid": v(-2.62, 5.5) * mm, "end": v(-3.2, 5.55) * mm});
            skArc(sketch, "E178.trimOffspring", {"start": v(-6.03, 2.95) * mm, "mid": v(-6.78, 2.5) * mm, "end": v(-7.5, 2) * mm});
            skArc(sketch, "E179.trimOffspring", {"start": v(-5.55, 3.2) * mm, "mid": v(-5.5, 2.62) * mm, "end": v(-5.42, 2.03) * mm});
            skArc(sketch, "E180.trimOffspring", {"start": v(-6.06, 3.5) * mm, "mid": v(-6.9, 3.02) * mm, "end": v(-7.68, 2.49) * mm});
            skArc(sketch, "E181.trimOffspring", {"start": v(-6.03, 2.95) * mm, "mid": v(-5.95, 2.26) * mm, "end": v(-5.84, 1.57) * mm});
            skArc(sketch, "E182.trimOffspring", {"start": v(-1.42, 5.3) * mm, "mid": v(-1.66, 5.09) * mm, "end": v(-1.89, 4.86) * mm});
            skArc(sketch, "E183.trimOffspring", {"start": v(-2.03, 5.42) * mm, "mid": v(-2.38, 5.07) * mm, "end": v(-2.72, 4.71) * mm});
            skArc(sketch, "E184.trimOffspring", {"start": v(-0.8, 5.15) * mm, "mid": v(-1.06, 5.05) * mm, "end": v(-1.32, 4.93) * mm});
            skArc(sketch, "E185.trimOffspring", {"start": v(-1.32, 4.93) * mm, "mid": v(-1.6, 4.9) * mm, "end": v(-1.89, 4.86) * mm});
            skArc(sketch, "E186.trimOffspring", {"start": v(-0.8, 5.15) * mm, "mid": v(-1.1, 5.23) * mm, "end": v(-1.42, 5.3) * mm});
            skArc(sketch, "E187.trimOffspring", {"start": v(0.95, 5.7) * mm, "mid": v(0.48, 6.07) * mm, "end": v(0, 6.4) * mm});
            skArc(sketch, "E188.trimOffspring", {"start": v(0.95, 5.7) * mm, "mid": v(0.47, 5.58) * mm, "end": v(0, 5.44) * mm});
            skArc(sketch, "E189.trimOffspring", {"start": v(0, 6.4) * mm, "mid": v(-0.48, 6.07) * mm, "end": v(-0.95, 5.7) * mm});
            skArc(sketch, "E190.trimOffspring", {"start": v(1.57, 5.84) * mm, "mid": v(1.02, 6.28) * mm, "end": v(0.46, 6.7) * mm});
            skArc(sketch, "E191.trimOffspring", {"start": v(1.42, 5.3) * mm, "mid": v(1.1, 5.23) * mm, "end": v(0.8, 5.15) * mm});
            skArc(sketch, "E192.trimOffspring", {"start": v(-0.46, 6.7) * mm, "mid": v(-1.22, 7.12) * mm, "end": v(-2, 7.5) * mm});
            skArc(sketch, "E193.trimOffspring", {"start": v(-0.46, 6.7) * mm, "mid": v(-1.02, 6.28) * mm, "end": v(-1.57, 5.84) * mm});
            skArc(sketch, "E194.trimOffspring", {"start": v(0, 7) * mm, "mid": v(-0.83, 7.48) * mm, "end": v(-1.69, 7.9) * mm});
            skArc(sketch, "E195.trimOffspring", {"start": v(3.27, -4.07) * mm, "mid": v(3.44, -3.84) * mm, "end": v(3.61, -3.61) * mm});
            skArc(sketch, "E196.trimOffspring", {"start": v(4.28, -4.28) * mm, "mid": v(4.93, -4.03) * mm, "end": v(5.57, -3.75) * mm});
            skArc(sketch, "E197.trimOffspring", {"start": v(3.75, -5.57) * mm, "mid": v(4.62, -5.56) * mm, "end": v(5.48, -5.48) * mm});
            skArc(sketch, "E198.trimOffspring", {"start": v(3.75, -5.57) * mm, "mid": v(4.03, -4.93) * mm, "end": v(4.28, -4.28) * mm});
            skArc(sketch, "E199.trimOffspring", {"start": v(3.5, -6.06) * mm, "mid": v(4.46, -6.06) * mm, "end": v(5.41, -6) * mm});
            skArc(sketch, "E200.trimOffspring", {"start": v(3.2, -5.55) * mm, "mid": v(3.45, -5.01) * mm, "end": v(3.67, -4.47) * mm});
            skArc(sketch, "E201.trimOffspring", {"start": v(3.88, -3.88) * mm, "mid": v(3.98, -3.58) * mm, "end": v(4.07, -3.27) * mm});
            skArc(sketch, "E202.trimOffspring", {"start": v(4.47, -3.67) * mm, "mid": v(4.6, -3.2) * mm, "end": v(4.71, -2.72) * mm});
            skArc(sketch, "E203.trimOffspring", {"start": v(4.47, -3.67) * mm, "mid": v(5.01, -3.45) * mm, "end": v(5.55, -3.2) * mm});
            skArc(sketch, "E204.trimOffspring", {"start": v(3.61, -3.61) * mm, "mid": v(3.84, -3.44) * mm, "end": v(4.07, -3.27) * mm});
            skArc(sketch, "E205.trimOffspring", {"start": v(4.71, -2.72) * mm, "mid": v(5.07, -2.38) * mm, "end": v(5.42, -2.03) * mm});
            skArc(sketch, "E206.trimOffspring", {"start": v(3.27, -4.07) * mm, "mid": v(3.58, -3.98) * mm, "end": v(3.88, -3.88) * mm});
            skArc(sketch, "E207.trimOffspring", {"start": v(5.3, 1.42) * mm, "mid": v(5.09, 1.66) * mm, "end": v(4.86, 1.89) * mm});
            skArc(sketch, "E208.trimOffspring", {"start": v(5.84, 1.57) * mm, "mid": v(5.95, 2.26) * mm, "end": v(6.03, 2.95) * mm});
            skArc(sketch, "E209.trimOffspring", {"start": v(4.93, 1.32) * mm, "mid": v(4.9, 1.6) * mm, "end": v(4.86, 1.89) * mm});
            skArc(sketch, "E210.trimOffspring", {"start": v(5.15, 0.8) * mm, "mid": v(5.23, 1.1) * mm, "end": v(5.3, 1.42) * mm});
            skArc(sketch, "E211.trimOffspring", {"start": v(5.42, 2.03) * mm, "mid": v(5.5, 2.62) * mm, "end": v(5.55, 3.2) * mm});
            skArc(sketch, "E212.trimOffspring", {"start": v(5.15, 0.8) * mm, "mid": v(5.05, 1.06) * mm, "end": v(4.93, 1.32) * mm});
            skArc(sketch, "E213.trimOffspring", {"start": v(5.44, 0) * mm, "mid": v(5.58, 0.47) * mm, "end": v(5.7, 0.95) * mm});
            skArc(sketch, "E214.trimOffspring", {"start": v(5.7, -0.95) * mm, "mid": v(6.07, -0.48) * mm, "end": v(6.4, 0) * mm});
            skArc(sketch, "E215.trimOffspring", {"start": v(6.4, 0) * mm, "mid": v(6.07, 0.48) * mm, "end": v(5.7, 0.95) * mm});
            skArc(sketch, "E216.trimOffspring", {"start": v(7, 0) * mm, "mid": v(7.48, 0.83) * mm, "end": v(7.9, 1.69) * mm});
            skArc(sketch, "E217.trimOffspring", {"start": v(6.7, 0.46) * mm, "mid": v(7.12, 1.22) * mm, "end": v(7.5, 2) * mm});
            skArc(sketch, "E218.trimOffspring", {"start": v(6.7, 0.46) * mm, "mid": v(6.28, 1.02) * mm, "end": v(5.84, 1.57) * mm});
            skArc(sketch, "E219.trimOffspring", {"start": v(5.7, -0.95) * mm, "mid": v(5.58, -0.47) * mm, "end": v(5.44, 0) * mm});
            skArc(sketch, "E220.trimOffspring", {"start": v(4.86, -1.89) * mm, "mid": v(4.9, -1.6) * mm, "end": v(4.93, -1.32) * mm});
            skArc(sketch, "E221.trimOffspring", {"start": v(5.3, -1.42) * mm, "mid": v(5.23, -1.1) * mm, "end": v(5.15, -0.8) * mm});
            skArc(sketch, "E222.trimOffspring", {"start": v(4.86, -1.89) * mm, "mid": v(5.09, -1.66) * mm, "end": v(5.3, -1.42) * mm});
            skArc(sketch, "E223.trimOffspring", {"start": v(4.93, -1.32) * mm, "mid": v(5.05, -1.06) * mm, "end": v(5.15, -0.8) * mm});
            skArc(sketch, "E224.trimOffspring", {"start": v(12.96, -6.95) * mm, "mid": v(14.7, -5.79) * mm, "end": v(16.23, -4.35) * mm});
            skArc(sketch, "E225.trimOffspring", {"start": v(12.47, -7.2) * mm, "mid": v(12.22, -5.35) * mm, "end": v(11.68, -3.56) * mm});
            skArc(sketch, "E226.trimOffspring", {"start": v(12.96, -6.95) * mm, "mid": v(12.66, -5.06) * mm, "end": v(12.1, -3.24) * mm});
            skArc(sketch, "E227.trimOffspring", {"start": v(13, -7.5) * mm, "mid": v(14.77, -6.37) * mm, "end": v(16.34, -4.96) * mm});
            skArc(sketch, "E228.trimOffspring", {"start": v(10.25, 0) * mm, "mid": v(11.16, 1.33) * mm, "end": v(11.9, 2.76) * mm});
            skArc(sketch, "E229.trimOffspring", {"start": v(9.92, 0.4) * mm, "mid": v(10.8, 1.69) * mm, "end": v(11.5, 3.08) * mm});
            skArc(sketch, "E230.trimOffspring", {"start": v(11.9, -2.76) * mm, "mid": v(13.25, -1.47) * mm, "end": v(14.4, 0) * mm});
            skArc(sketch, "E231.trimOffspring", {"start": v(12.1, -3.24) * mm, "mid": v(13.5, -1.95) * mm, "end": v(14.7, -0.46) * mm});
            skArc(sketch, "E232.trimOffspring", {"start": v(8.8, -4.62) * mm, "mid": v(8.5, -3.38) * mm, "end": v(8.1, -2.17) * mm});
            skArc(sketch, "E233.trimOffspring", {"start": v(9.6, 0) * mm, "mid": v(8.8, 0.89) * mm, "end": v(7.9, 1.69) * mm});
            skArc(sketch, "E234.trimOffspring", {"start": v(7.9, -1.69) * mm, "mid": v(7.48, -0.83) * mm, "end": v(7, 0) * mm});
            skArc(sketch, "E235.trimOffspring", {"start": v(11.5, -3.08) * mm, "mid": v(10.8, -1.69) * mm, "end": v(9.92, -0.4) * mm});
            skArc(sketch, "E236.trimOffspring", {"start": v(9.92, 0.4) * mm, "mid": v(9.05, 1.33) * mm, "end": v(8.1, 2.17) * mm});
            skArc(sketch, "E237.trimOffspring", {"start": v(7.5, -2) * mm, "mid": v(7.12, -1.22) * mm, "end": v(6.7, -0.46) * mm});
            skArc(sketch, "E238.trimOffspring", {"start": v(8.32, -4.8) * mm, "mid": v(8.06, -3.63) * mm, "end": v(7.68, -2.49) * mm});
            skArc(sketch, "E239.trimOffspring", {"start": v(8.1, -2.17) * mm, "mid": v(9.05, -1.33) * mm, "end": v(9.92, -0.4) * mm});
            skArc(sketch, "E240.trimOffspring", {"start": v(7.5, 2) * mm, "mid": v(6.78, 2.5) * mm, "end": v(6.03, 2.95) * mm});
            skArc(sketch, "E241.trimOffspring", {"start": v(7.68, 2.49) * mm, "mid": v(6.9, 3.02) * mm, "end": v(6.06, 3.5) * mm});
            skArc(sketch, "E242.trimOffspring", {"start": v(6.06, 3.5) * mm, "mid": v(6.06, 4.46) * mm, "end": v(6, 5.41) * mm});
            skArc(sketch, "E243.trimOffspring", {"start": v(8.87, 5.12) * mm, "mid": v(9, 6.73) * mm, "end": v(8.92, 8.34) * mm});
            skArc(sketch, "E244.trimOffspring", {"start": v(8.4, 5.3) * mm, "mid": v(8.5, 6.86) * mm, "end": v(8.41, 8.41) * mm});
            skArc(sketch, "E245.trimOffspring", {"start": v(7.68, 2.49) * mm, "mid": v(8.06, 3.63) * mm, "end": v(8.32, 4.8) * mm});
            skArc(sketch, "E246.trimOffspring", {"start": v(11.68, 3.56) * mm, "mid": v(12.22, 5.35) * mm, "end": v(12.47, 7.2) * mm});
            skArc(sketch, "E247.trimOffspring", {"start": v(8.1, 2.17) * mm, "mid": v(8.5, 3.38) * mm, "end": v(8.8, 4.62) * mm});
            skArc(sketch, "E248.trimOffspring", {"start": v(8.32, 4.8) * mm, "mid": v(7.17, 5.16) * mm, "end": v(6, 5.41) * mm});
            skArc(sketch, "E249.trimOffspring", {"start": v(8.4, 5.3) * mm, "mid": v(7.18, 5.68) * mm, "end": v(5.93, 5.93) * mm});
            skArc(sketch, "E250.trimOffspring", {"start": v(12.1, 3.24) * mm, "mid": v(12.66, 5.06) * mm, "end": v(12.96, 6.95) * mm});
            skArc(sketch, "E251.trimOffspring", {"start": v(11.68, 3.56) * mm, "mid": v(10.33, 4.43) * mm, "end": v(8.87, 5.12) * mm});
            skArc(sketch, "E252.trimOffspring", {"start": v(11.5, 3.08) * mm, "mid": v(10.19, 3.93) * mm, "end": v(8.8, 4.62) * mm});
            skArc(sketch, "E253.trimOffspring", {"start": v(12.5, 7.75) * mm, "mid": v(10.72, 8.44) * mm, "end": v(8.86, 8.86) * mm});
            skArc(sketch, "E254.trimOffspring", {"start": v(12.5, 7.75) * mm, "mid": v(12.36, 9.84) * mm, "end": v(11.88, 11.88) * mm});
            skArc(sketch, "E255.trimOffspring", {"start": v(13, 7.5) * mm, "mid": v(12.9, 9.6) * mm, "end": v(12.47, 11.67) * mm});
            skArc(sketch, "E256.trimOffspring", {"start": v(5.84, -1.57) * mm, "mid": v(6.28, -1.02) * mm, "end": v(6.7, -0.46) * mm});
            skArc(sketch, "E257.trimOffspring", {"start": v(7.9, -1.69) * mm, "mid": v(8.8, -0.89) * mm, "end": v(9.6, 0) * mm});
            skArc(sketch, "E258.trimOffspring", {"start": v(5.55, 3.2) * mm, "mid": v(5.01, 3.45) * mm, "end": v(4.47, 3.67) * mm});
            skArc(sketch, "E259.trimOffspring", {"start": v(5.57, 3.75) * mm, "mid": v(4.93, 4.03) * mm, "end": v(4.28, 4.28) * mm});
            skArc(sketch, "E260.trimOffspring", {"start": v(5.42, 2.03) * mm, "mid": v(5.07, 2.38) * mm, "end": v(4.71, 2.72) * mm});
            skArc(sketch, "E261.trimOffspring", {"start": v(4.71, 2.72) * mm, "mid": v(4.6, 3.2) * mm, "end": v(4.47, 3.67) * mm});
            skArc(sketch, "E262.trimOffspring", {"start": v(4.07, 3.27) * mm, "mid": v(3.84, 3.44) * mm, "end": v(3.61, 3.61) * mm});
            skArc(sketch, "E263.trimOffspring", {"start": v(4.28, 4.28) * mm, "mid": v(4.03, 4.93) * mm, "end": v(3.75, 5.57) * mm});
            skArc(sketch, "E264.trimOffspring", {"start": v(3.88, 3.88) * mm, "mid": v(3.58, 3.98) * mm, "end": v(3.27, 4.07) * mm});
            skArc(sketch, "E265.trimOffspring", {"start": v(3.67, 4.47) * mm, "mid": v(3.2, 4.6) * mm, "end": v(2.72, 4.71) * mm});
            skArc(sketch, "E266.trimOffspring", {"start": v(3.67, 4.47) * mm, "mid": v(3.45, 5.01) * mm, "end": v(3.2, 5.55) * mm});
            skArc(sketch, "E267.trimOffspring", {"start": v(4.07, 3.27) * mm, "mid": v(3.98, 3.58) * mm, "end": v(3.88, 3.88) * mm});
            skArc(sketch, "E268.trimOffspring", {"start": v(1.89, 4.86) * mm, "mid": v(1.6, 4.9) * mm, "end": v(1.32, 4.93) * mm});
            skArc(sketch, "E269.trimOffspring", {"start": v(3.61, 3.61) * mm, "mid": v(3.44, 3.84) * mm, "end": v(3.27, 4.07) * mm});
            skArc(sketch, "E270.trimOffspring", {"start": v(1.32, 4.93) * mm, "mid": v(1.06, 5.05) * mm, "end": v(0.8, 5.15) * mm});
            skArc(sketch, "E271.trimOffspring", {"start": v(1.89, 4.86) * mm, "mid": v(1.66, 5.09) * mm, "end": v(1.42, 5.3) * mm});
            skArc(sketch, "E272.trimOffspring", {"start": v(2.72, 4.71) * mm, "mid": v(2.38, 5.07) * mm, "end": v(2.03, 5.42) * mm});
            skArc(sketch, "E273.trimOffspring", {"start": v(5.93, 5.93) * mm, "mid": v(5.68, 7.18) * mm, "end": v(5.3, 8.4) * mm});
            skArc(sketch, "E274.trimOffspring", {"start": v(5.57, 3.75) * mm, "mid": v(5.56, 4.62) * mm, "end": v(5.48, 5.48) * mm});
            skArc(sketch, "E275.trimOffspring", {"start": v(3.5, 6.06) * mm, "mid": v(3.02, 6.9) * mm, "end": v(2.49, 7.68) * mm});
            skArc(sketch, "E276.trimOffspring", {"start": v(1.69, 7.9) * mm, "mid": v(0.89, 8.8) * mm, "end": v(0, 9.6) * mm});
            skArc(sketch, "E277.trimOffspring", {"start": v(2.17, 8.1) * mm, "mid": v(1.33, 9.05) * mm, "end": v(0.4, 9.92) * mm});
            skArc(sketch, "E278.trimOffspring", {"start": v(5.41, 6) * mm, "mid": v(4.46, 6.06) * mm, "end": v(3.5, 6.06) * mm});
            skArc(sketch, "E279.trimOffspring", {"start": v(2.95, 6.03) * mm, "mid": v(2.26, 5.95) * mm, "end": v(1.57, 5.84) * mm});
            skArc(sketch, "E280.trimOffspring", {"start": v(2.95, 6.03) * mm, "mid": v(2.5, 6.78) * mm, "end": v(2, 7.5) * mm});
            skArc(sketch, "E281.trimOffspring", {"start": v(3.2, 5.55) * mm, "mid": v(2.62, 5.5) * mm, "end": v(2.03, 5.42) * mm});
            skArc(sketch, "E282.trimOffspring", {"start": v(5.41, 6) * mm, "mid": v(5.16, 7.17) * mm, "end": v(4.8, 8.32) * mm});
            skArc(sketch, "E283.trimOffspring", {"start": v(5.48, 5.48) * mm, "mid": v(4.62, 5.56) * mm, "end": v(3.75, 5.57) * mm});
            skArc(sketch, "E284.trimOffspring", {"start": v(-6.7, -0.46) * mm, "mid": v(-6.28, -1.02) * mm, "end": v(-5.84, -1.57) * mm});
            skArc(sketch, "E285.trimOffspring", {"start": v(-7.5, 2) * mm, "mid": v(-7.12, 1.22) * mm, "end": v(-6.7, 0.46) * mm});
            skArc(sketch, "E286.trimOffspring", {"start": v(-7.9, 1.69) * mm, "mid": v(-7.48, 0.83) * mm, "end": v(-7, 0) * mm});
            skArc(sketch, "E287.trimOffspring", {"start": v(-2.17, -8.1) * mm, "mid": v(-1.33, -9.05) * mm, "end": v(-0.4, -9.92) * mm});
            skArc(sketch, "E288.trimOffspring", {"start": v(-1.69, -7.9) * mm, "mid": v(-0.89, -8.8) * mm, "end": v(0, -9.6) * mm});
            skArc(sketch, "E289.trimOffspring", {"start": v(-2, -7.5) * mm, "mid": v(-1.22, -7.12) * mm, "end": v(-0.46, -6.7) * mm});
            skArc(sketch, "E290.trimOffspring", {"start": v(-1.69, -7.9) * mm, "mid": v(-0.83, -7.48) * mm, "end": v(0, -7) * mm});
            skArc(sketch, "E291.trimOffspring", {"start": v(-4.62, -8.8) * mm, "mid": v(-3.93, -10.19) * mm, "end": v(-3.08, -11.5) * mm});
            skArc(sketch, "E292.trimOffspring", {"start": v(-4.62, -8.8) * mm, "mid": v(-3.38, -8.5) * mm, "end": v(-2.17, -8.1) * mm});
            skArc(sketch, "E293.trimOffspring", {"start": v(-4.8, -8.32) * mm, "mid": v(-3.63, -8.06) * mm, "end": v(-2.49, -7.68) * mm});
            skArc(sketch, "E294.trimOffspring", {"start": v(-5.12, -8.87) * mm, "mid": v(-4.43, -10.33) * mm, "end": v(-3.56, -11.68) * mm});
            skArc(sketch, "E295.trimOffspring", {"start": v(-5.48, -5.48) * mm, "mid": v(-4.62, -5.56) * mm, "end": v(-3.75, -5.57) * mm});
            skArc(sketch, "E296.trimOffspring", {"start": v(-5.93, -5.93) * mm, "mid": v(-5.68, -7.18) * mm, "end": v(-5.3, -8.4) * mm});
            skArc(sketch, "E297.trimOffspring", {"start": v(-5.41, -6) * mm, "mid": v(-5.16, -7.17) * mm, "end": v(-4.8, -8.32) * mm});
            skArc(sketch, "E298.trimOffspring", {"start": v(-5.41, -6) * mm, "mid": v(-4.46, -6.06) * mm, "end": v(-3.5, -6.06) * mm});
            skArc(sketch, "E299.trimOffspring", {"start": v(-2.95, -6.03) * mm, "mid": v(-2.26, -5.95) * mm, "end": v(-1.57, -5.84) * mm});
            skArc(sketch, "E300.trimOffspring", {"start": v(-8.32, -4.8) * mm, "mid": v(-7.17, -5.16) * mm, "end": v(-6, -5.41) * mm});
            skArc(sketch, "E301.trimOffspring", {"start": v(-8.4, -5.3) * mm, "mid": v(-7.18, -5.68) * mm, "end": v(-5.93, -5.93) * mm});
            skArc(sketch, "E302.trimOffspring", {"start": v(-11.5, -3.08) * mm, "mid": v(-10.19, -3.93) * mm, "end": v(-8.8, -4.62) * mm});
            skArc(sketch, "E303.trimOffspring", {"start": v(-11.68, -3.56) * mm, "mid": v(-10.33, -4.43) * mm, "end": v(-8.87, -5.12) * mm});
            skArc(sketch, "E304.trimOffspring", {"start": v(-8.4, -5.3) * mm, "mid": v(-8.5, -6.86) * mm, "end": v(-8.41, -8.41) * mm});
            skArc(sketch, "E305.trimOffspring", {"start": v(-8.87, -5.12) * mm, "mid": v(-9, -6.73) * mm, "end": v(-8.92, -8.34) * mm});
            skArc(sketch, "E306.trimOffspring", {"start": v(-12.1, -3.24) * mm, "mid": v(-12.66, -5.06) * mm, "end": v(-12.96, -6.95) * mm});
            skArc(sketch, "E307.trimOffspring", {"start": v(-11.68, -3.56) * mm, "mid": v(-12.22, -5.35) * mm, "end": v(-12.47, -7.2) * mm});
            skArc(sketch, "E308.trimOffspring", {"start": v(-12.47, -7.2) * mm, "mid": v(-10.74, -7.9) * mm, "end": v(-8.92, -8.34) * mm});
            skArc(sketch, "E309.trimOffspring", {"start": v(-11.88, -11.88) * mm, "mid": v(-9.84, -12.36) * mm, "end": v(-7.75, -12.5) * mm});
            skArc(sketch, "E310.trimOffspring", {"start": v(-8.34, -8.92) * mm, "mid": v(-6.73, -9) * mm, "end": v(-5.12, -8.87) * mm});
            skArc(sketch, "E311.trimOffspring", {"start": v(-7.2, -12.47) * mm, "mid": v(-5.35, -12.22) * mm, "end": v(-3.56, -11.68) * mm});
            skArc(sketch, "E312.trimOffspring", {"start": v(-2.76, -11.9) * mm, "mid": v(-1.33, -11.16) * mm, "end": v(0, -10.25) * mm});
            skArc(sketch, "E313.trimOffspring", {"start": v(0.46, -14.7) * mm, "mid": v(2.34, -15.63) * mm, "end": v(4.35, -16.23) * mm});
            skArc(sketch, "E314.trimOffspring", {"start": v(-4.35, -16.23) * mm, "mid": v(-0.42, -14.67) * mm, "end": v(2.76, -11.9) * mm});
            skArc(sketch, "E315.trimOffspring", {"start": v(0, -19.3) * mm, "mid": v(1.24, -19.63) * mm, "end": v(2.5, -19.84) * mm});
            skArc(sketch, "E316.trimOffspring", {"start": v(4.5, -16.77) * mm, "mid": v(6.65, -17) * mm, "end": v(8.82, -16.86) * mm});
            skArc(sketch, "E317.trimOffspring", {"start": v(7.5, -13) * mm, "mid": v(9.6, -12.9) * mm, "end": v(11.67, -12.47) * mm});
            skArc(sketch, "E318.trimOffspring", {"start": v(3.56, -11.68) * mm, "mid": v(4.43, -10.33) * mm, "end": v(5.12, -8.87) * mm});
            skArc(sketch, "E319.trimOffspring", {"start": v(0.4, -9.92) * mm, "mid": v(1.33, -9.05) * mm, "end": v(2.17, -8.1) * mm});
            skArc(sketch, "E320.trimOffspring", {"start": v(12.47, -11.67) * mm, "mid": v(12.9, -9.6) * mm, "end": v(13, -7.5) * mm});
            skArc(sketch, "E321.trimOffspring", {"start": v(10.2, -16.07) * mm, "mid": v(12.13, -15.37) * mm, "end": v(13.92, -14.36) * mm});
            skArc(sketch, "E322.trimOffspring", {"start": v(19.84, -2.5) * mm, "mid": v(20, 0) * mm, "end": v(19.84, 2.5) * mm});
            skArc(sketch, "E323.trimOffspring", {"start": v(16.64, -3.87) * mm, "mid": v(17.88, -2.03) * mm, "end": v(18.77, 0) * mm});
            skArc(sketch, "E324.trimOffspring", {"start": v(16.64, -3.87) * mm, "mid": v(15.98, -1.87) * mm, "end": v(15, 0) * mm});
            skArc(sketch, "E325.trimOffspring", {"start": v(16.77, -4.5) * mm, "mid": v(18.05, -2.74) * mm, "end": v(19.01, -0.8) * mm});
            skArc(sketch, "E326.trimOffspring", {"start": v(11.9, -2.76) * mm, "mid": v(11.16, -1.33) * mm, "end": v(10.25, 0) * mm});
            skArc(sketch, "E327.trimOffspring", {"start": v(14.4, 0) * mm, "mid": v(13.25, 1.47) * mm, "end": v(11.9, 2.76) * mm});
            skArc(sketch, "E328.trimOffspring", {"start": v(14.7, 0.46) * mm, "mid": v(13.5, 1.95) * mm, "end": v(12.1, 3.24) * mm});
            skArc(sketch, "E329.trimOffspring", {"start": v(15, 0) * mm, "mid": v(15.98, 1.87) * mm, "end": v(16.64, 3.87) * mm});
            skArc(sketch, "E330.trimOffspring", {"start": v(14.7, 0.46) * mm, "mid": v(15.63, 2.34) * mm, "end": v(16.23, 4.35) * mm});
            skArc(sketch, "E331.trimOffspring", {"start": v(8.86, 8.86) * mm, "mid": v(8.44, 10.72) * mm, "end": v(7.75, 12.5) * mm});
            skArc(sketch, "E332.trimOffspring", {"start": v(5.12, 8.87) * mm, "mid": v(4.43, 10.33) * mm, "end": v(3.56, 11.68) * mm});
            skArc(sketch, "E333.trimOffspring", {"start": v(8.34, 8.92) * mm, "mid": v(6.73, 9) * mm, "end": v(5.12, 8.87) * mm});
            skArc(sketch, "E334.trimOffspring", {"start": v(4.62, 8.8) * mm, "mid": v(3.93, 10.19) * mm, "end": v(3.08, 11.5) * mm});
            skArc(sketch, "E335.trimOffspring", {"start": v(8.41, 8.41) * mm, "mid": v(6.86, 8.5) * mm, "end": v(5.3, 8.4) * mm});
            skArc(sketch, "E336.trimOffspring", {"start": v(4.62, 8.8) * mm, "mid": v(3.38, 8.5) * mm, "end": v(2.17, 8.1) * mm});
            skArc(sketch, "E337.trimOffspring", {"start": v(4.8, 8.32) * mm, "mid": v(3.63, 8.06) * mm, "end": v(2.49, 7.68) * mm});
            skArc(sketch, "E338.trimOffspring", {"start": v(8.34, 8.92) * mm, "mid": v(7.9, 10.74) * mm, "end": v(7.2, 12.47) * mm});
            skArc(sketch, "E339.trimOffspring", {"start": v(2, 7.5) * mm, "mid": v(1.22, 7.12) * mm, "end": v(0.46, 6.7) * mm});
            skArc(sketch, "E340.trimOffspring", {"start": v(1.69, 7.9) * mm, "mid": v(0.83, 7.48) * mm, "end": v(0, 7) * mm});
            skArc(sketch, "E341.trimOffspring", {"start": v(-8.92, 8.34) * mm, "mid": v(-9, 6.73) * mm, "end": v(-8.87, 5.12) * mm});
            skArc(sketch, "E342.trimOffspring", {"start": v(-4.8, 8.32) * mm, "mid": v(-5.16, 7.17) * mm, "end": v(-5.41, 6) * mm});
            skArc(sketch, "E343.trimOffspring", {"start": v(-9.6, 0) * mm, "mid": v(-8.8, -0.89) * mm, "end": v(-7.9, -1.69) * mm});
            skArc(sketch, "E344.trimOffspring", {"start": v(-11.9, 2.76) * mm, "mid": v(-14.67, -0.42) * mm, "end": v(-16.23, -4.35) * mm});
            skArc(sketch, "E345.trimOffspring", {"start": v(-8.8, 4.62) * mm, "mid": v(-8.5, 3.38) * mm, "end": v(-8.1, 2.17) * mm});
            skArc(sketch, "E346.trimOffspring", {"start": v(-14.4, 0) * mm, "mid": v(-13.25, -1.47) * mm, "end": v(-11.9, -2.76) * mm});
            skArc(sketch, "E347.trimOffspring", {"start": v(-16.64, 3.87) * mm, "mid": v(-15.98, 1.87) * mm, "end": v(-15, 0) * mm});
            skArc(sketch, "E348.trimOffspring", {"start": v(-12.96, 6.95) * mm, "mid": v(-12.66, 5.06) * mm, "end": v(-12.1, 3.24) * mm});
            skArc(sketch, "E349.trimOffspring", {"start": v(-8.92, 8.34) * mm, "mid": v(-10.74, 7.9) * mm, "end": v(-12.47, 7.2) * mm});
            skArc(sketch, "E350.trimOffspring", {"start": v(-12.96, 6.95) * mm, "mid": v(-16.52, 4.02) * mm, "end": v(-18.77, 0) * mm});
            skArc(sketch, "E351.trimOffspring", {"start": v(-13, 7.5) * mm, "mid": v(-16.6, 4.69) * mm, "end": v(-19.01, 0.8) * mm});
            skArc(sketch, "E352.trimOffspring", {"start": v(-8.32, 4.8) * mm, "mid": v(-8.06, 3.63) * mm, "end": v(-7.68, 2.49) * mm});
            skArc(sketch, "E353.trimOffspring", {"start": v(-5.48, 5.48) * mm, "mid": v(-5.56, 4.62) * mm, "end": v(-5.57, 3.75) * mm});
            skArc(sketch, "E354.trimOffspring", {"start": v(-6, 5.41) * mm, "mid": v(-6.06, 4.46) * mm, "end": v(-6.06, 3.5) * mm});
            skArc(sketch, "E355.trimOffspring", {"start": v(-6, 5.41) * mm, "mid": v(-7.17, 5.16) * mm, "end": v(-8.32, 4.8) * mm});
            skArc(sketch, "E356.trimOffspring", {"start": v(-5.93, 5.93) * mm, "mid": v(-7.18, 5.68) * mm, "end": v(-8.4, 5.3) * mm});
            skArc(sketch, "E357.trimOffspring", {"start": v(-3.88, 3.88) * mm, "mid": v(-3.98, 3.58) * mm, "end": v(-4.07, 3.27) * mm});
            skArc(sketch, "E358.trimOffspring", {"start": v(-11.67, -12.47) * mm, "mid": v(-9.6, -12.9) * mm, "end": v(-7.5, -13) * mm});
            skArc(sketch, "E359.trimOffspring", {"start": v(-8.41, -8.41) * mm, "mid": v(-6.86, -8.5) * mm, "end": v(-5.3, -8.4) * mm});
            skArc(sketch, "E360.trimOffspring", {"start": v(-12.5, -7.75) * mm, "mid": v(-10.72, -8.44) * mm, "end": v(-8.86, -8.86) * mm});
            skArc(sketch, "E361.trimOffspring", {"start": v(-11.67, -12.47) * mm, "mid": v(-10.7, -14.47) * mm, "end": v(-9.39, -16.26) * mm});
            skArc(sketch, "E362.trimOffspring", {"start": v(-6.95, -12.96) * mm, "mid": v(-5.06, -12.66) * mm, "end": v(-3.24, -12.1) * mm});
            skArc(sketch, "E363.trimOffspring", {"start": v(-7.5, -13) * mm, "mid": v(-6.37, -14.77) * mm, "end": v(-4.96, -16.34) * mm});
            skArc(sketch, "E364.trimOffspring", {"start": v(-12.28, -12.28) * mm, "mid": v(-11.4, -14.26) * mm, "end": v(-10.2, -16.07) * mm});
            skArc(sketch, "E365.trimOffspring", {"start": v(-8.34, -8.92) * mm, "mid": v(-7.9, -10.74) * mm, "end": v(-7.2, -12.47) * mm});
            skArc(sketch, "E366.trimOffspring", {"start": v(-8.86, -8.86) * mm, "mid": v(-8.44, -10.72) * mm, "end": v(-7.75, -12.5) * mm});
            skArc(sketch, "E367.trimOffspring", {"start": v(-12.5, -7.75) * mm, "mid": v(-12.36, -9.84) * mm, "end": v(-11.88, -11.88) * mm});
            skArc(sketch, "E368.trimOffspring", {"start": v(-13, -7.5) * mm, "mid": v(-12.9, -9.6) * mm, "end": v(-12.47, -11.67) * mm});
            skArc(sketch, "E369.trimOffspring", {"start": v(-8.82, -16.86) * mm, "mid": v(-7.25, -18.19) * mm, "end": v(-5.48, -19.23) * mm});
            skArc(sketch, "E370.trimOffspring", {"start": v(-8.82, -16.86) * mm, "mid": v(-6.65, -17) * mm, "end": v(-4.5, -16.77) * mm});
            skArc(sketch, "E371.trimOffspring", {"start": v(-9.65, -16.71) * mm, "mid": v(-8.74, -17.62) * mm, "end": v(-7.75, -18.44) * mm});
            skArc(sketch, "E372.trimOffspring", {"start": v(-9.39, -16.26) * mm, "mid": v(-7.18, -16.5) * mm, "end": v(-4.96, -16.34) * mm});
            skArc(sketch, "E373.trimOffspring", {"start": v(-4.5, -16.77) * mm, "mid": v(-2.74, -18.05) * mm, "end": v(-0.8, -19.01) * mm});
            skArc(sketch, "E374.trimOffspring", {"start": v(-3.87, -16.64) * mm, "mid": v(-1.87, -15.98) * mm, "end": v(0, -15) * mm});
            skArc(sketch, "E375.trimOffspring", {"start": v(-3.87, -16.64) * mm, "mid": v(-2.03, -17.88) * mm, "end": v(0, -18.77) * mm});
            skArc(sketch, "E376.trimOffspring", {"start": v(-6.95, -12.96) * mm, "mid": v(-5.79, -14.7) * mm, "end": v(-4.35, -16.23) * mm});
            skArc(sketch, "E377.trimOffspring", {"start": v(-3.08, -11.5) * mm, "mid": v(-1.69, -10.8) * mm, "end": v(-0.4, -9.92) * mm});
            skArc(sketch, "E378.trimOffspring", {"start": v(0, -18.77) * mm, "mid": v(2.03, -17.88) * mm, "end": v(3.87, -16.64) * mm});
            skArc(sketch, "E379.trimOffspring", {"start": v(0, -15) * mm, "mid": v(1.87, -15.98) * mm, "end": v(3.87, -16.64) * mm});
            skArc(sketch, "E380.trimOffspring", {"start": v(-2.76, -11.9) * mm, "mid": v(-1.47, -13.25) * mm, "end": v(0, -14.4) * mm});
            skArc(sketch, "E381.trimOffspring", {"start": v(0.46, -14.7) * mm, "mid": v(1.95, -13.5) * mm, "end": v(3.24, -12.1) * mm});
            skArc(sketch, "E382.trimOffspring", {"start": v(-3.24, -12.1) * mm, "mid": v(-1.95, -13.5) * mm, "end": v(-0.46, -14.7) * mm});
            skArc(sketch, "E383.trimOffspring", {"start": v(0, -10.25) * mm, "mid": v(1.33, -11.16) * mm, "end": v(2.76, -11.9) * mm});
            skArc(sketch, "E384.trimOffspring", {"start": v(0.4, -9.92) * mm, "mid": v(1.69, -10.8) * mm, "end": v(3.08, -11.5) * mm});
            skArc(sketch, "E385.trimOffspring", {"start": v(0, -9.6) * mm, "mid": v(0.89, -8.8) * mm, "end": v(1.69, -7.9) * mm});
            skArc(sketch, "E386.trimOffspring", {"start": v(2.17, -8.1) * mm, "mid": v(3.38, -8.5) * mm, "end": v(4.62, -8.8) * mm});
            skArc(sketch, "E387.trimOffspring", {"start": v(4.8, -8.32) * mm, "mid": v(5.16, -7.17) * mm, "end": v(5.41, -6) * mm});
            skArc(sketch, "E388.trimOffspring", {"start": v(2.49, -7.68) * mm, "mid": v(3.63, -8.06) * mm, "end": v(4.8, -8.32) * mm});
            skArc(sketch, "E389.trimOffspring", {"start": v(5.12, -8.87) * mm, "mid": v(6.73, -9) * mm, "end": v(8.34, -8.92) * mm});
            skArc(sketch, "E390.trimOffspring", {"start": v(3.08, -11.5) * mm, "mid": v(3.93, -10.19) * mm, "end": v(4.62, -8.8) * mm});
            skArc(sketch, "E391.trimOffspring", {"start": v(16.23, -4.35) * mm, "mid": v(15.63, -2.34) * mm, "end": v(14.7, -0.46) * mm});
            skArc(sketch, "E392.trimOffspring", {"start": v(18.77, 0) * mm, "mid": v(17.88, 2.03) * mm, "end": v(16.64, 3.87) * mm});
            skArc(sketch, "E393.trimOffspring", {"start": v(19.01, 0.8) * mm, "mid": v(18.05, 2.74) * mm, "end": v(16.77, 4.5) * mm});
            skArc(sketch, "E394.trimOffspring", {"start": v(19.3, 0) * mm, "mid": v(19.63, 1.24) * mm, "end": v(19.84, 2.5) * mm});
            skArc(sketch, "E395.trimOffspring", {"start": v(19.01, 0.8) * mm, "mid": v(19.37, 2.82) * mm, "end": v(19.4, 4.87) * mm});
            skArc(sketch, "E396.trimOffspring", {"start": v(2.49, -7.68) * mm, "mid": v(3.02, -6.9) * mm, "end": v(3.5, -6.06) * mm});
            skArc(sketch, "E397.trimOffspring", {"start": v(3.24, -12.1) * mm, "mid": v(5.06, -12.66) * mm, "end": v(6.95, -12.96) * mm});
            skArc(sketch, "E398.trimOffspring", {"start": v(3.56, -11.68) * mm, "mid": v(5.35, -12.22) * mm, "end": v(7.2, -12.47) * mm});
            skArc(sketch, "E399.trimOffspring", {"start": v(2, -7.5) * mm, "mid": v(2.5, -6.78) * mm, "end": v(2.95, -6.03) * mm});
            skArc(sketch, "E400.trimOffspring", {"start": v(5.3, -8.4) * mm, "mid": v(6.86, -8.5) * mm, "end": v(8.41, -8.41) * mm});
            skArc(sketch, "E401.trimOffspring", {"start": v(5.3, -8.4) * mm, "mid": v(5.68, -7.18) * mm, "end": v(5.93, -5.93) * mm});
            skArc(sketch, "E402.trimOffspring", {"start": v(5.93, -5.93) * mm, "mid": v(7.18, -5.68) * mm, "end": v(8.4, -5.3) * mm});
            skArc(sketch, "E403.trimOffspring", {"start": v(6.06, -3.5) * mm, "mid": v(6.9, -3.02) * mm, "end": v(7.68, -2.49) * mm});
            skArc(sketch, "E404.trimOffspring", {"start": v(6.03, -2.95) * mm, "mid": v(6.78, -2.5) * mm, "end": v(7.5, -2) * mm});
            skArc(sketch, "E405.trimOffspring", {"start": v(8.8, -4.62) * mm, "mid": v(10.19, -3.93) * mm, "end": v(11.5, -3.08) * mm});
            skArc(sketch, "E406.trimOffspring", {"start": v(8.87, -5.12) * mm, "mid": v(10.33, -4.43) * mm, "end": v(11.68, -3.56) * mm});
            skArc(sketch, "E407.trimOffspring", {"start": v(6, -5.41) * mm, "mid": v(7.17, -5.16) * mm, "end": v(8.32, -4.8) * mm});
            skArc(sketch, "E408.trimOffspring", {"start": v(6.03, -2.95) * mm, "mid": v(5.95, -2.26) * mm, "end": v(5.84, -1.57) * mm});
            skArc(sketch, "E409.trimOffspring", {"start": v(5.55, -3.2) * mm, "mid": v(5.5, -2.62) * mm, "end": v(5.42, -2.03) * mm});
            skArc(sketch, "E410.trimOffspring", {"start": v(6, -5.41) * mm, "mid": v(6.06, -4.46) * mm, "end": v(6.06, -3.5) * mm});
            skArc(sketch, "E411.trimOffspring", {"start": v(5.48, -5.48) * mm, "mid": v(5.56, -4.62) * mm, "end": v(5.57, -3.75) * mm});
            skArc(sketch, "E412.trimOffspring", {"start": v(8.92, -8.34) * mm, "mid": v(9, -6.73) * mm, "end": v(8.87, -5.12) * mm});
            skArc(sketch, "E413.trimOffspring", {"start": v(8.92, -8.34) * mm, "mid": v(10.74, -7.9) * mm, "end": v(12.47, -7.2) * mm});
            skArc(sketch, "E414.trimOffspring", {"start": v(8.41, -8.41) * mm, "mid": v(8.5, -6.86) * mm, "end": v(8.4, -5.3) * mm});
            skArc(sketch, "E415.trimOffspring", {"start": v(8.86, -8.86) * mm, "mid": v(10.72, -8.44) * mm, "end": v(12.5, -7.75) * mm});
            skArc(sketch, "E416.trimOffspring", {"start": v(7.75, -12.5) * mm, "mid": v(9.84, -12.36) * mm, "end": v(11.88, -11.88) * mm});
            skArc(sketch, "E417.trimOffspring", {"start": v(7.75, -12.5) * mm, "mid": v(8.44, -10.72) * mm, "end": v(8.86, -8.86) * mm});
            skArc(sketch, "E418.trimOffspring", {"start": v(11.88, -11.88) * mm, "mid": v(12.36, -9.84) * mm, "end": v(12.5, -7.75) * mm});
            skArc(sketch, "E419.trimOffspring", {"start": v(12.47, -11.67) * mm, "mid": v(14.47, -10.7) * mm, "end": v(16.26, -9.39) * mm});
            skArc(sketch, "E420.trimOffspring", {"start": v(7.2, -12.47) * mm, "mid": v(7.9, -10.74) * mm, "end": v(8.34, -8.92) * mm});
            skArc(sketch, "E421.trimOffspring", {"start": v(-16.34, -4.96) * mm, "mid": v(-14.77, -6.37) * mm, "end": v(-13, -7.5) * mm});
            skArc(sketch, "E422.trimOffspring", {"start": v(-16.26, -9.39) * mm, "mid": v(-14.47, -10.7) * mm, "end": v(-12.47, -11.67) * mm});
            skArc(sketch, "E423.trimOffspring", {"start": v(-16.34, -4.96) * mm, "mid": v(-16.5, -7.18) * mm, "end": v(-16.26, -9.39) * mm});
            skArc(sketch, "E424.trimOffspring", {"start": v(-14.7, -0.46) * mm, "mid": v(-13.5, -1.95) * mm, "end": v(-12.1, -3.24) * mm});
            skArc(sketch, "E425.trimOffspring", {"start": v(-16.77, -4.5) * mm, "mid": v(-17, -6.65) * mm, "end": v(-16.86, -8.82) * mm});
            skArc(sketch, "E426.trimOffspring", {"start": v(-15, 0) * mm, "mid": v(-15.98, -1.87) * mm, "end": v(-16.64, -3.87) * mm});
            skArc(sketch, "E427.trimOffspring", {"start": v(-11.9, 2.76) * mm, "mid": v(-11.16, 1.33) * mm, "end": v(-10.25, 0) * mm});
            skArc(sketch, "E428.trimOffspring", {"start": v(-8.1, 2.17) * mm, "mid": v(-9.05, 1.33) * mm, "end": v(-9.92, 0.4) * mm});
            skArc(sketch, "E429.trimOffspring", {"start": v(-11.5, 3.08) * mm, "mid": v(-10.8, 1.69) * mm, "end": v(-9.92, 0.4) * mm});
            skArc(sketch, "E430.trimOffspring", {"start": v(-12.1, 3.24) * mm, "mid": v(-13.5, 1.95) * mm, "end": v(-14.7, 0.46) * mm});
            skArc(sketch, "E431.trimOffspring", {"start": v(-8.8, 4.62) * mm, "mid": v(-10.19, 3.93) * mm, "end": v(-11.5, 3.08) * mm});
            skArc(sketch, "E432.trimOffspring", {"start": v(-8.87, 5.12) * mm, "mid": v(-10.33, 4.43) * mm, "end": v(-11.68, 3.56) * mm});
            skArc(sketch, "E433.trimOffspring", {"start": v(-9.92, -0.4) * mm, "mid": v(-9.05, -1.33) * mm, "end": v(-8.1, -2.17) * mm});
            skArc(sketch, "E434.trimOffspring", {"start": v(-10.25, 0) * mm, "mid": v(-11.16, -1.33) * mm, "end": v(-11.9, -2.76) * mm});
            skArc(sketch, "E435.trimOffspring", {"start": v(-9.92, -0.4) * mm, "mid": v(-10.8, -1.69) * mm, "end": v(-11.5, -3.08) * mm});
            skArc(sketch, "E436.trimOffspring", {"start": v(-7.9, 1.69) * mm, "mid": v(-8.8, 0.89) * mm, "end": v(-9.6, 0) * mm});
            skArc(sketch, "E437.trimOffspring", {"start": v(-16.07, -10.2) * mm, "mid": v(-14.26, -11.4) * mm, "end": v(-12.28, -12.28) * mm});
            skArc(sketch, "E438.trimOffspring", {"start": v(-16.07, -10.2) * mm, "mid": v(-15.37, -12.13) * mm, "end": v(-14.36, -13.92) * mm});
            skArc(sketch, "E439.trimOffspring", {"start": v(-16.71, -9.65) * mm, "mid": v(-16.38, -10.89) * mm, "end": v(-15.93, -12.1) * mm});
            skArc(sketch, "E440.trimOffspring", {"start": v(-16.23, -4.35) * mm, "mid": v(-14.7, -5.79) * mm, "end": v(-12.96, -6.95) * mm});
            skArc(sketch, "E441.trimOffspring", {"start": v(0.8, -19.01) * mm, "mid": v(2.74, -18.05) * mm, "end": v(4.5, -16.77) * mm});
            skArc(sketch, "E442.trimOffspring", {"start": v(4.35, -16.23) * mm, "mid": v(5.79, -14.7) * mm, "end": v(6.95, -12.96) * mm});
            skArc(sketch, "E443.trimOffspring", {"start": v(0.8, -19.01) * mm, "mid": v(2.82, -19.37) * mm, "end": v(4.87, -19.4) * mm});
            skArc(sketch, "E444.trimOffspring", {"start": v(4.96, -16.34) * mm, "mid": v(6.37, -14.77) * mm, "end": v(7.5, -13) * mm});
            skArc(sketch, "E445.trimOffspring", {"start": v(4.96, -16.34) * mm, "mid": v(7.18, -16.5) * mm, "end": v(9.39, -16.26) * mm});
            skArc(sketch, "E446.trimOffspring", {"start": v(9.39, -16.26) * mm, "mid": v(10.7, -14.47) * mm, "end": v(11.67, -12.47) * mm});
            skArc(sketch, "E447.trimOffspring", {"start": v(9.65, -16.71) * mm, "mid": v(10.89, -16.38) * mm, "end": v(12.1, -15.93) * mm});
            skArc(sketch, "E448.trimOffspring", {"start": v(10.2, -16.07) * mm, "mid": v(11.4, -14.26) * mm, "end": v(12.28, -12.28) * mm});
            skArc(sketch, "E449.trimOffspring", {"start": v(12.28, -12.28) * mm, "mid": v(14.26, -11.4) * mm, "end": v(16.07, -10.2) * mm});
            skArc(sketch, "E450.trimOffspring", {"start": v(16.26, -9.39) * mm, "mid": v(16.5, -7.18) * mm, "end": v(16.34, -4.96) * mm});
            skArc(sketch, "E451.trimOffspring", {"start": v(16.86, -8.82) * mm, "mid": v(17, -6.65) * mm, "end": v(16.77, -4.5) * mm});
            skArc(sketch, "E452.trimOffspring", {"start": v(16.86, -8.82) * mm, "mid": v(18.19, -7.25) * mm, "end": v(19.23, -5.48) * mm});
            skArc(sketch, "E453.trimOffspring", {"start": v(16.71, -9.65) * mm, "mid": v(17.62, -8.74) * mm, "end": v(18.44, -7.75) * mm});
            skArc(sketch, "E454.trimOffspring", {"start": v(16.23, 4.35) * mm, "mid": v(14.7, 5.79) * mm, "end": v(12.96, 6.95) * mm});
            skArc(sketch, "E455.trimOffspring", {"start": v(16.77, 4.5) * mm, "mid": v(17, 6.65) * mm, "end": v(16.86, 8.82) * mm});
            skArc(sketch, "E456.trimOffspring", {"start": v(16.34, 4.96) * mm, "mid": v(14.77, 6.37) * mm, "end": v(13, 7.5) * mm});
            skArc(sketch, "E457.trimOffspring", {"start": v(16.34, 4.96) * mm, "mid": v(16.5, 7.18) * mm, "end": v(16.26, 9.39) * mm});
            skArc(sketch, "E458.trimOffspring", {"start": v(16.71, 9.65) * mm, "mid": v(16.38, 10.89) * mm, "end": v(15.93, 12.1) * mm});
            skArc(sketch, "E459.trimOffspring", {"start": v(16.26, 9.39) * mm, "mid": v(14.47, 10.7) * mm, "end": v(12.47, 11.67) * mm});
            skArc(sketch, "E460.trimOffspring", {"start": v(11.67, 12.47) * mm, "mid": v(10.7, 14.47) * mm, "end": v(9.39, 16.26) * mm});
            skArc(sketch, "E461.trimOffspring", {"start": v(11.88, 11.88) * mm, "mid": v(9.84, 12.36) * mm, "end": v(7.75, 12.5) * mm});
            skArc(sketch, "E462.trimOffspring", {"start": v(16.07, 10.2) * mm, "mid": v(15.37, 12.13) * mm, "end": v(14.36, 13.92) * mm});
            skArc(sketch, "E463.trimOffspring", {"start": v(16.07, 10.2) * mm, "mid": v(14.26, 11.4) * mm, "end": v(12.28, 12.28) * mm});
            skArc(sketch, "E464.trimOffspring", {"start": v(12.28, 12.28) * mm, "mid": v(11.4, 14.26) * mm, "end": v(10.2, 16.07) * mm});
            skArc(sketch, "E465.trimOffspring", {"start": v(11.67, 12.47) * mm, "mid": v(9.6, 12.9) * mm, "end": v(7.5, 13) * mm});
            skArc(sketch, "E466.trimOffspring", {"start": v(12.47, 7.2) * mm, "mid": v(10.74, 7.9) * mm, "end": v(8.92, 8.34) * mm});
            skArc(sketch, "E467.trimOffspring", {"start": v(-1.57, 5.84) * mm, "mid": v(-2.26, 5.95) * mm, "end": v(-2.95, 6.03) * mm});
            skCircle(sketch, "E468", {"center": v(-16, 16) * mm, "radius": 2.5 * mm});
            skCircle(sketch, "E469", {"center": v(16, 16) * mm, "radius": 2.5 * mm});
            skCircle(sketch, "E470", {"center": v(-16, -16) * mm, "radius": 4.5 * mm});
            skCircle(sketch, "E471", {"center": v(16, -16) * mm, "radius": 4.5 * mm});
            skCircle(sketch, "E472.converted", {"center": v(16, 16) * mm, "radius": 1.75 * mm});
            skCircle(sketch, "E473.converted", {"center": v(-16, 16) * mm, "radius": 1.75 * mm});
            skSolve(sketch);
        }
        {
            var Q0;
            Q0=makeQuery(id+"F0.imprint","IMPRINT",FACE,{"disambiguationData":[TD([[makeQuery(id+"F0.imprint","IMPRINT",EDGE,{"derivedFrom":sQuery(id+"F0.wireOp",EDGE,"E1")}),1.0]])]});
            extrude(context, id + "F1", {"entities" : qUnion([Q0]), "depth" : 1 * mm, "offsetDistance" : 25 * mm, "hasSecondDirection" : true, "secondDirectionOppositeDirection" : true, "secondDirectionDepth" : 1 * mm});
        }
        {
            var Q0;
            Q0=makeQuery(id+"F1.opExtrude","CAP_FACE",FACE,{"disambiguationData":[OSD([sQuery(id+"F0.wireOp",EDGE,"E0"),sQuery(id+"F0.wireOp",EDGE,"E1"),sQuery(id+"F0.wireOp",EDGE,"E2.1.0"),sQuery(id+"F0.wireOp",EDGE,"E2.2.0"),sQuery(id+"F0.wireOp",EDGE,"E2.3.0"),sQuery(id+"F0.wireOp",EDGE,"E2.4.0"),sQuery(id+"F0.wireOp",EDGE,"E2.5.0"),sQuery(id+"F0.wireOp",EDGE,"E2.6.0"),sQuery(id+"F0.wireOp",EDGE,"E2.7.0"),sQuery(id+"F0.wireOp",EDGE,"E2.8.0"),sQuery(id+"F0.wireOp",EDGE,"E2.9.0"),sQuery(id+"F0.wireOp",EDGE,"E2.10.0"),sQuery(id+"F0.wireOp",EDGE,"E2.11.0"),sQuery(id+"F0.wireOp",EDGE,"E3"),sQuery(id+"F0.wireOp",EDGE,"E8.trimOffspring"),sQuery(id+"F0.wireOp",EDGE,"E10"),sQuery(id+"F0.wireOp",EDGE,"E11"),sQuery(id+"F0.wireOp",EDGE,"E12.1.0"),sQuery(id+"F0.wireOp",EDGE,"E12.2.0"),sQuery(id+"F0.wireOp",EDGE,"E12.3.0"),sQuery(id+"F0.wireOp",EDGE,"E12.4.0"),sQuery(id+"F0.wireOp",EDGE,"E12.5.0"),sQuery(id+"F0.wireOp",EDGE,"E12.6.0"),sQuery(id+"F0.wireOp",EDGE,"E12.7.0"),sQuery(id+"F0.wireOp",EDGE,"E12.8.0"),sQuery(id+"F0.wireOp",EDGE,"E12.9.0"),sQuery(id+"F0.wireOp",EDGE,"E12.10.0"),sQuery(id+"F0.wireOp",EDGE,"E12.11.0"),sQuery(id+"F0.wireOp",EDGE,"E13"),sQuery(id+"F0.wireOp",EDGE,"E14.trimOffspring"),sQuery(id+"F0.wireOp",EDGE,"E15.trimOffspring"),sQuery(id+"F0.wireOp",EDGE,"E16.trimOffspring"),sQuery(id+"F0.wireOp",EDGE,"E17.trimOffspring"),sQuery(id+"F0.wireOp",EDGE,"E18.trimOffspring"),sQuery(id+"F0.wireOp",EDGE,"E19.trimOffspring"),sQuery(id+"F0.wireOp",EDGE,"E20.trimOffspring"),sQuery(id+"F0.wireOp",EDGE,"E21.trimOffspring"),sQuery(id+"F0.wireOp",EDGE,"E22.trimOffspring"),sQuery(id+"F0.wireOp",EDGE,"E23.trimOffspring"),sQuery(id+"F0.wireOp",EDGE,"E24.trimOffspring"),sQuery(id+"F0.wireOp",EDGE,"E25.trimOffspring"),sQuery(id+"F0.wireOp",EDGE,"E26.trimOffspring"),sQuery(id+"F0.wireOp",EDGE,"E27.trimOffspring"),sQuery(id+"F0.wireOp",EDGE,"E28.trimOffspring"),sQuery(id+"F0.wireOp",EDGE,"E29.trimOffspring"),sQuery(id+"F0.wireOp",EDGE,"E30.trimOffspring"),sQuery(id+"F0.wireOp",EDGE,"E31.trimOffspring"),sQuery(id+"F0.wireOp",EDGE,"E32.trimOffspring"),sQuery(id+"F0.wireOp",EDGE,"E33.trimOffspring"),sQuery(id+"F0.wireOp",EDGE,"E34.trimOffspring"),sQuery(id+"F0.wireOp",EDGE,"E38.trimOffspring"),sQuery(id+"F0.wireOp",EDGE,"E39.trimOffspring"),sQuery(id+"F0.wireOp",EDGE,"E40.trimOffspring"),sQuery(id+"F0.wireOp",EDGE,"E41.trimOffspring"),sQuery(id+"F0.wireOp",EDGE,"E42.trimOffspring"),sQuery(id+"F0.wireOp",EDGE,"E43.trimOffspring"),sQuery(id+"F0.wireOp",EDGE,"E45.trimOffspring"),sQuery(id+"F0.wireOp",EDGE,"E46.trimOffspring"),sQuery(id+"F0.wireOp",EDGE,"E48.trimOffspring"),sQuery(id+"F0.wireOp",EDGE,"E49.trimOffspring"),sQuery(id+"F0.wireOp",EDGE,"E50.trimOffspring"),sQuery(id+"F0.wireOp",EDGE,"E51.trimOffspring"),sQuery(id+"F0.wireOp",EDGE,"E52.trimOffspring"),sQuery(id+"F0.wireOp",EDGE,"E53.trimOffspring"),sQuery(id+"F0.wireOp",EDGE,"E54.trimOffspring"),sQuery(id+"F0.wireOp",EDGE,"E55.trimOffspring"),sQuery(id+"F0.wireOp",EDGE,"E56.trimOffspring"),sQuery(id+"F0.wireOp",EDGE,"E57.trimOffspring"),sQuery(id+"F0.wireOp",EDGE,"E58.trimOffspring"),sQuery(id+"F0.wireOp",EDGE,"E59.trimOffspring"),sQuery(id+"F0.wireOp",EDGE,"E60.trimOffspring"),sQuery(id+"F0.wireOp",EDGE,"E61.trimOffspring"),sQuery(id+"F0.wireOp",EDGE,"E62.trimOffspring"),sQuery(id+"F0.wireOp",EDGE,"E63.trimOffspring"),sQuery(id+"F0.wireOp",EDGE,"E64.trimOffspring"),sQuery(id+"F0.wireOp",EDGE,"E65.trimOffspring"),sQuery(id+"F0.wireOp",EDGE,"E66.trimOffspring"),sQuery(id+"F0.wireOp",EDGE,"E67.trimOffspring"),sQuery(id+"F0.wireOp",EDGE,"E68.trimOffspring"),sQuery(id+"F0.wireOp",EDGE,"E69.trimOffspring"),sQuery(id+"F0.wireOp",EDGE,"E70.trimOffspring"),sQuery(id+"F0.wireOp",EDGE,"E71.trimOffspring"),sQuery(id+"F0.wireOp",EDGE,"E72.trimOffspring"),sQuery(id+"F0.wireOp",EDGE,"E73.trimOffspring"),sQuery(id+"F0.wireOp",EDGE,"E74.trimOffspring"),sQuery(id+"F0.wireOp",EDGE,"E75.trimOffspring"),sQuery(id+"F0.wireOp",EDGE,"E76.trimOffspring"),sQuery(id+"F0.wireOp",EDGE,"E77.trimOffspring"),sQuery(id+"F0.wireOp",EDGE,"E78.trimOffspring"),sQuery(id+"F0.wireOp",EDGE,"E79.trimOffspring"),sQuery(id+"F0.wireOp",EDGE,"E80.trimOffspring"),sQuery(id+"F0.wireOp",EDGE,"E81.trimOffspring"),sQuery(id+"F0.wireOp",EDGE,"E82.trimOffspring"),sQuery(id+"F0.wireOp",EDGE,"E83.trimOffspring"),sQuery(id+"F0.wireOp",EDGE,"E84.trimOffspring"),sQuery(id+"F0.wireOp",EDGE,"E85.trimOffspring"),sQuery(id+"F0.wireOp",EDGE,"E86.trimOffspring"),sQuery(id+"F0.wireOp",EDGE,"E87.trimOffspring"),sQuery(id+"F0.wireOp",EDGE,"E88.trimOffspring"),sQuery(id+"F0.wireOp",EDGE,"E89.trimOffspring"),sQuery(id+"F0.wireOp",EDGE,"E90.trimOffspring"),sQuery(id+"F0.wireOp",EDGE,"E91.trimOffspring"),sQuery(id+"F0.wireOp",EDGE,"E92.trimOffspring"),sQuery(id+"F0.wireOp",EDGE,"E93.trimOffspring"),sQuery(id+"F0.wireOp",EDGE,"E94.trimOffspring"),sQuery(id+"F0.wireOp",EDGE,"E95.trimOffspring"),sQuery(id+"F0.wireOp",EDGE,"E96.trimOffspring"),sQuery(id+"F0.wireOp",EDGE,"E97.trimOffspring"),sQuery(id+"F0.wireOp",EDGE,"E98.trimOffspring"),sQuery(id+"F0.wireOp",EDGE,"E99.trimOffspring"),sQuery(id+"F0.wireOp",EDGE,"E100.trimOffspring"),sQuery(id+"F0.wireOp",EDGE,"E101.trimOffspring"),sQuery(id+"F0.wireOp",EDGE,"E102.trimOffspring"),sQuery(id+"F0.wireOp",EDGE,"E103.trimOffspring"),sQuery(id+"F0.wireOp",EDGE,"E104.trimOffspring"),sQuery(id+"F0.wireOp",EDGE,"E105.trimOffspring"),sQuery(id+"F0.wireOp",EDGE,"E106.trimOffspring"),sQuery(id+"F0.wireOp",EDGE,"E107.trimOffspring"),sQuery(id+"F0.wireOp",EDGE,"E108.trimOffspring"),sQuery(id+"F0.wireOp",EDGE,"E109.trimOffspring"),sQuery(id+"F0.wireOp",EDGE,"E110.trimOffspring"),sQuery(id+"F0.wireOp",EDGE,"E111.trimOffspring"),sQuery(id+"F0.wireOp",EDGE,"E112.trimOffspring"),sQuery(id+"F0.wireOp",EDGE,"E113.trimOffspring"),sQuery(id+"F0.wireOp",EDGE,"E114.trimOffspring"),sQuery(id+"F0.wireOp",EDGE,"E115.trimOffspring"),sQuery(id+"F0.wireOp",EDGE,"E116.trimOffspring"),sQuery(id+"F0.wireOp",EDGE,"E117.trimOffspring"),sQuery(id+"F0.wireOp",EDGE,"E118.trimOffspring"),sQuery(id+"F0.wireOp",EDGE,"E119.trimOffspring"),sQuery(id+"F0.wireOp",EDGE,"E120.trimOffspring"),sQuery(id+"F0.wireOp",EDGE,"E121.trimOffspring"),sQuery(id+"F0.wireOp",EDGE,"E122.trimOffspring"),sQuery(id+"F0.wireOp",EDGE,"E123.trimOffspring"),sQuery(id+"F0.wireOp",EDGE,"E124.trimOffspring"),sQuery(id+"F0.wireOp",EDGE,"E125.trimOffspring"),sQuery(id+"F0.wireOp",EDGE,"E126.trimOffspring"),sQuery(id+"F0.wireOp",EDGE,"E127.trimOffspring"),sQuery(id+"F0.wireOp",EDGE,"E128.trimOffspring"),sQuery(id+"F0.wireOp",EDGE,"E129.trimOffspring"),sQuery(id+"F0.wireOp",EDGE,"E130.trimOffspring"),sQuery(id+"F0.wireOp",EDGE,"E131.trimOffspring"),sQuery(id+"F0.wireOp",EDGE,"E132.trimOffspring"),sQuery(id+"F0.wireOp",EDGE,"E133.trimOffspring"),sQuery(id+"F0.wireOp",EDGE,"E134.trimOffspring"),sQuery(id+"F0.wireOp",EDGE,"E135.trimOffspring"),sQuery(id+"F0.wireOp",EDGE,"E136.trimOffspring"),sQuery(id+"F0.wireOp",EDGE,"E137.trimOffspring"),sQuery(id+"F0.wireOp",EDGE,"E138.trimOffspring"),sQuery(id+"F0.wireOp",EDGE,"E139.trimOffspring"),sQuery(id+"F0.wireOp",EDGE,"E140.trimOffspring"),sQuery(id+"F0.wireOp",EDGE,"E141.trimOffspring"),sQuery(id+"F0.wireOp",EDGE,"E142.trimOffspring"),sQuery(id+"F0.wireOp",EDGE,"E143.trimOffspring"),sQuery(id+"F0.wireOp",EDGE,"E144.trimOffspring"),sQuery(id+"F0.wireOp",EDGE,"E145.trimOffspring"),sQuery(id+"F0.wireOp",EDGE,"E146.trimOffspring"),sQuery(id+"F0.wireOp",EDGE,"E147.trimOffspring"),sQuery(id+"F0.wireOp",EDGE,"E148.trimOffspring"),sQuery(id+"F0.wireOp",EDGE,"E149.trimOffspring"),sQuery(id+"F0.wireOp",EDGE,"E150.trimOffspring"),sQuery(id+"F0.wireOp",EDGE,"E151.trimOffspring"),sQuery(id+"F0.wireOp",EDGE,"E152.trimOffspring"),sQuery(id+"F0.wireOp",EDGE,"E153.trimOffspring"),sQuery(id+"F0.wireOp",EDGE,"E154.trimOffspring"),sQuery(id+"F0.wireOp",EDGE,"E155.trimOffspring"),sQuery(id+"F0.wireOp",EDGE,"E156.trimOffspring"),sQuery(id+"F0.wireOp",EDGE,"E157.trimOffspring"),sQuery(id+"F0.wireOp",EDGE,"E158.trimOffspring"),sQuery(id+"F0.wireOp",EDGE,"E159.trimOffspring"),sQuery(id+"F0.wireOp",EDGE,"E160.trimOffspring"),sQuery(id+"F0.wireOp",EDGE,"E161.trimOffspring"),sQuery(id+"F0.wireOp",EDGE,"E162.trimOffspring"),sQuery(id+"F0.wireOp",EDGE,"E163.trimOffspring"),sQuery(id+"F0.wireOp",EDGE,"E164.trimOffspring"),sQuery(id+"F0.wireOp",EDGE,"E165.trimOffspring"),sQuery(id+"F0.wireOp",EDGE,"E166.trimOffspring"),sQuery(id+"F0.wireOp",EDGE,"E167.trimOffspring"),sQuery(id+"F0.wireOp",EDGE,"E168.trimOffspring"),sQuery(id+"F0.wireOp",EDGE,"E169.trimOffspring"),sQuery(id+"F0.wireOp",EDGE,"E170.trimOffspring"),sQuery(id+"F0.wireOp",EDGE,"E171.trimOffspring"),sQuery(id+"F0.wireOp",EDGE,"E172.trimOffspring"),sQuery(id+"F0.wireOp",EDGE,"E173.trimOffspring"),sQuery(id+"F0.wireOp",EDGE,"E174.trimOffspring"),sQuery(id+"F0.wireOp",EDGE,"E175.trimOffspring"),sQuery(id+"F0.wireOp",EDGE,"E176.trimOffspring"),sQuery(id+"F0.wireOp",EDGE,"E177.trimOffspring"),sQuery(id+"F0.wireOp",EDGE,"E178.trimOffspring"),sQuery(id+"F0.wireOp",EDGE,"E179.trimOffspring"),sQuery(id+"F0.wireOp",EDGE,"E180.trimOffspring"),sQuery(id+"F0.wireOp",EDGE,"E181.trimOffspring"),sQuery(id+"F0.wireOp",EDGE,"E182.trimOffspring"),sQuery(id+"F0.wireOp",EDGE,"E183.trimOffspring"),sQuery(id+"F0.wireOp",EDGE,"E184.trimOffspring"),sQuery(id+"F0.wireOp",EDGE,"E185.trimOffspring"),sQuery(id+"F0.wireOp",EDGE,"E186.trimOffspring"),sQuery(id+"F0.wireOp",EDGE,"E187.trimOffspring"),sQuery(id+"F0.wireOp",EDGE,"E188.trimOffspring"),sQuery(id+"F0.wireOp",EDGE,"E189.trimOffspring"),sQuery(id+"F0.wireOp",EDGE,"E190.trimOffspring"),sQuery(id+"F0.wireOp",EDGE,"E191.trimOffspring"),sQuery(id+"F0.wireOp",EDGE,"E192.trimOffspring"),sQuery(id+"F0.wireOp",EDGE,"E193.trimOffspring"),sQuery(id+"F0.wireOp",EDGE,"E194.trimOffspring"),sQuery(id+"F0.wireOp",EDGE,"E195.trimOffspring"),sQuery(id+"F0.wireOp",EDGE,"E196.trimOffspring"),sQuery(id+"F0.wireOp",EDGE,"E197.trimOffspring"),sQuery(id+"F0.wireOp",EDGE,"E198.trimOffspring"),sQuery(id+"F0.wireOp",EDGE,"E199.trimOffspring"),sQuery(id+"F0.wireOp",EDGE,"E200.trimOffspring"),sQuery(id+"F0.wireOp",EDGE,"E201.trimOffspring"),sQuery(id+"F0.wireOp",EDGE,"E202.trimOffspring"),sQuery(id+"F0.wireOp",EDGE,"E203.trimOffspring"),sQuery(id+"F0.wireOp",EDGE,"E204.trimOffspring"),sQuery(id+"F0.wireOp",EDGE,"E205.trimOffspring"),sQuery(id+"F0.wireOp",EDGE,"E206.trimOffspring"),sQuery(id+"F0.wireOp",EDGE,"E207.trimOffspring"),sQuery(id+"F0.wireOp",EDGE,"E208.trimOffspring"),sQuery(id+"F0.wireOp",EDGE,"E209.trimOffspring"),sQuery(id+"F0.wireOp",EDGE,"E210.trimOffspring"),sQuery(id+"F0.wireOp",EDGE,"E211.trimOffspring"),sQuery(id+"F0.wireOp",EDGE,"E212.trimOffspring"),sQuery(id+"F0.wireOp",EDGE,"E213.trimOffspring"),sQuery(id+"F0.wireOp",EDGE,"E214.trimOffspring"),sQuery(id+"F0.wireOp",EDGE,"E215.trimOffspring"),sQuery(id+"F0.wireOp",EDGE,"E216.trimOffspring"),sQuery(id+"F0.wireOp",EDGE,"E217.trimOffspring"),sQuery(id+"F0.wireOp",EDGE,"E218.trimOffspring"),sQuery(id+"F0.wireOp",EDGE,"E219.trimOffspring"),sQuery(id+"F0.wireOp",EDGE,"E220.trimOffspring"),sQuery(id+"F0.wireOp",EDGE,"E221.trimOffspring"),sQuery(id+"F0.wireOp",EDGE,"E222.trimOffspring"),sQuery(id+"F0.wireOp",EDGE,"E223.trimOffspring"),sQuery(id+"F0.wireOp",EDGE,"E224.trimOffspring"),sQuery(id+"F0.wireOp",EDGE,"E225.trimOffspring"),sQuery(id+"F0.wireOp",EDGE,"E226.trimOffspring"),sQuery(id+"F0.wireOp",EDGE,"E227.trimOffspring"),sQuery(id+"F0.wireOp",EDGE,"E228.trimOffspring"),sQuery(id+"F0.wireOp",EDGE,"E229.trimOffspring"),sQuery(id+"F0.wireOp",EDGE,"E230.trimOffspring"),sQuery(id+"F0.wireOp",EDGE,"E231.trimOffspring"),sQuery(id+"F0.wireOp",EDGE,"E232.trimOffspring"),sQuery(id+"F0.wireOp",EDGE,"E233.trimOffspring"),sQuery(id+"F0.wireOp",EDGE,"E234.trimOffspring"),sQuery(id+"F0.wireOp",EDGE,"E235.trimOffspring"),sQuery(id+"F0.wireOp",EDGE,"E236.trimOffspring"),sQuery(id+"F0.wireOp",EDGE,"E237.trimOffspring"),sQuery(id+"F0.wireOp",EDGE,"E238.trimOffspring"),sQuery(id+"F0.wireOp",EDGE,"E239.trimOffspring"),sQuery(id+"F0.wireOp",EDGE,"E240.trimOffspring"),sQuery(id+"F0.wireOp",EDGE,"E241.trimOffspring"),sQuery(id+"F0.wireOp",EDGE,"E242.trimOffspring"),sQuery(id+"F0.wireOp",EDGE,"E243.trimOffspring"),sQuery(id+"F0.wireOp",EDGE,"E244.trimOffspring"),sQuery(id+"F0.wireOp",EDGE,"E245.trimOffspring"),sQuery(id+"F0.wireOp",EDGE,"E246.trimOffspring"),sQuery(id+"F0.wireOp",EDGE,"E247.trimOffspring"),sQuery(id+"F0.wireOp",EDGE,"E248.trimOffspring"),sQuery(id+"F0.wireOp",EDGE,"E249.trimOffspring"),sQuery(id+"F0.wireOp",EDGE,"E250.trimOffspring"),sQuery(id+"F0.wireOp",EDGE,"E251.trimOffspring"),sQuery(id+"F0.wireOp",EDGE,"E252.trimOffspring"),sQuery(id+"F0.wireOp",EDGE,"E253.trimOffspring"),sQuery(id+"F0.wireOp",EDGE,"E254.trimOffspring"),sQuery(id+"F0.wireOp",EDGE,"E255.trimOffspring"),sQuery(id+"F0.wireOp",EDGE,"E256.trimOffspring"),sQuery(id+"F0.wireOp",EDGE,"E257.trimOffspring"),sQuery(id+"F0.wireOp",EDGE,"E258.trimOffspring"),sQuery(id+"F0.wireOp",EDGE,"E259.trimOffspring"),sQuery(id+"F0.wireOp",EDGE,"E260.trimOffspring"),sQuery(id+"F0.wireOp",EDGE,"E261.trimOffspring"),sQuery(id+"F0.wireOp",EDGE,"E262.trimOffspring"),sQuery(id+"F0.wireOp",EDGE,"E263.trimOffspring"),sQuery(id+"F0.wireOp",EDGE,"E264.trimOffspring"),sQuery(id+"F0.wireOp",EDGE,"E265.trimOffspring"),sQuery(id+"F0.wireOp",EDGE,"E266.trimOffspring"),sQuery(id+"F0.wireOp",EDGE,"E267.trimOffspring"),sQuery(id+"F0.wireOp",EDGE,"E268.trimOffspring"),sQuery(id+"F0.wireOp",EDGE,"E269.trimOffspring"),sQuery(id+"F0.wireOp",EDGE,"E270.trimOffspring"),sQuery(id+"F0.wireOp",EDGE,"E271.trimOffspring"),sQuery(id+"F0.wireOp",EDGE,"E272.trimOffspring"),sQuery(id+"F0.wireOp",EDGE,"E273.trimOffspring"),sQuery(id+"F0.wireOp",EDGE,"E274.trimOffspring"),sQuery(id+"F0.wireOp",EDGE,"E275.trimOffspring"),sQuery(id+"F0.wireOp",EDGE,"E276.trimOffspring"),sQuery(id+"F0.wireOp",EDGE,"E277.trimOffspring"),sQuery(id+"F0.wireOp",EDGE,"E278.trimOffspring"),sQuery(id+"F0.wireOp",EDGE,"E279.trimOffspring"),sQuery(id+"F0.wireOp",EDGE,"E280.trimOffspring"),sQuery(id+"F0.wireOp",EDGE,"E281.trimOffspring"),sQuery(id+"F0.wireOp",EDGE,"E282.trimOffspring"),sQuery(id+"F0.wireOp",EDGE,"E283.trimOffspring"),sQuery(id+"F0.wireOp",EDGE,"E284.trimOffspring"),sQuery(id+"F0.wireOp",EDGE,"E285.trimOffspring"),sQuery(id+"F0.wireOp",EDGE,"E286.trimOffspring"),sQuery(id+"F0.wireOp",EDGE,"E287.trimOffspring"),sQuery(id+"F0.wireOp",EDGE,"E288.trimOffspring"),sQuery(id+"F0.wireOp",EDGE,"E289.trimOffspring"),sQuery(id+"F0.wireOp",EDGE,"E290.trimOffspring"),sQuery(id+"F0.wireOp",EDGE,"E291.trimOffspring"),sQuery(id+"F0.wireOp",EDGE,"E292.trimOffspring"),sQuery(id+"F0.wireOp",EDGE,"E293.trimOffspring"),sQuery(id+"F0.wireOp",EDGE,"E294.trimOffspring"),sQuery(id+"F0.wireOp",EDGE,"E295.trimOffspring"),sQuery(id+"F0.wireOp",EDGE,"E296.trimOffspring"),sQuery(id+"F0.wireOp",EDGE,"E297.trimOffspring"),sQuery(id+"F0.wireOp",EDGE,"E298.trimOffspring"),sQuery(id+"F0.wireOp",EDGE,"E299.trimOffspring"),sQuery(id+"F0.wireOp",EDGE,"E300.trimOffspring"),sQuery(id+"F0.wireOp",EDGE,"E301.trimOffspring"),sQuery(id+"F0.wireOp",EDGE,"E302.trimOffspring"),sQuery(id+"F0.wireOp",EDGE,"E303.trimOffspring"),sQuery(id+"F0.wireOp",EDGE,"E304.trimOffspring"),sQuery(id+"F0.wireOp",EDGE,"E305.trimOffspring"),sQuery(id+"F0.wireOp",EDGE,"E306.trimOffspring"),sQuery(id+"F0.wireOp",EDGE,"E307.trimOffspring"),sQuery(id+"F0.wireOp",EDGE,"E308.trimOffspring"),sQuery(id+"F0.wireOp",EDGE,"E309.trimOffspring"),sQuery(id+"F0.wireOp",EDGE,"E310.trimOffspring"),sQuery(id+"F0.wireOp",EDGE,"E311.trimOffspring"),sQuery(id+"F0.wireOp",EDGE,"E312.trimOffspring"),sQuery(id+"F0.wireOp",EDGE,"E313.trimOffspring"),sQuery(id+"F0.wireOp",EDGE,"E314.trimOffspring"),sQuery(id+"F0.wireOp",EDGE,"E315.trimOffspring"),sQuery(id+"F0.wireOp",EDGE,"E316.trimOffspring"),sQuery(id+"F0.wireOp",EDGE,"E317.trimOffspring"),sQuery(id+"F0.wireOp",EDGE,"E318.trimOffspring"),sQuery(id+"F0.wireOp",EDGE,"E319.trimOffspring"),sQuery(id+"F0.wireOp",EDGE,"E320.trimOffspring"),sQuery(id+"F0.wireOp",EDGE,"E321.trimOffspring"),sQuery(id+"F0.wireOp",EDGE,"E35.trimOffspring"),sQuery(id+"F0.wireOp",EDGE,"E322.trimOffspring"),sQuery(id+"F0.wireOp",EDGE,"E323.trimOffspring"),sQuery(id+"F0.wireOp",EDGE,"E324.trimOffspring"),sQuery(id+"F0.wireOp",EDGE,"E325.trimOffspring"),sQuery(id+"F0.wireOp",EDGE,"E326.trimOffspring"),sQuery(id+"F0.wireOp",EDGE,"E327.trimOffspring"),sQuery(id+"F0.wireOp",EDGE,"E328.trimOffspring"),sQuery(id+"F0.wireOp",EDGE,"E329.trimOffspring"),sQuery(id+"F0.wireOp",EDGE,"E330.trimOffspring"),sQuery(id+"F0.wireOp",EDGE,"E331.trimOffspring"),sQuery(id+"F0.wireOp",EDGE,"E332.trimOffspring"),sQuery(id+"F0.wireOp",EDGE,"E333.trimOffspring"),sQuery(id+"F0.wireOp",EDGE,"E334.trimOffspring"),sQuery(id+"F0.wireOp",EDGE,"E335.trimOffspring"),sQuery(id+"F0.wireOp",EDGE,"E336.trimOffspring"),sQuery(id+"F0.wireOp",EDGE,"E337.trimOffspring"),sQuery(id+"F0.wireOp",EDGE,"E338.trimOffspring"),sQuery(id+"F0.wireOp",EDGE,"E339.trimOffspring"),sQuery(id+"F0.wireOp",EDGE,"E340.trimOffspring"),sQuery(id+"F0.wireOp",EDGE,"E341.trimOffspring"),sQuery(id+"F0.wireOp",EDGE,"E342.trimOffspring"),sQuery(id+"F0.wireOp",EDGE,"E343.trimOffspring"),sQuery(id+"F0.wireOp",EDGE,"E344.trimOffspring"),sQuery(id+"F0.wireOp",EDGE,"E345.trimOffspring"),sQuery(id+"F0.wireOp",EDGE,"E346.trimOffspring"),sQuery(id+"F0.wireOp",EDGE,"E347.trimOffspring"),sQuery(id+"F0.wireOp",EDGE,"E348.trimOffspring"),sQuery(id+"F0.wireOp",EDGE,"E349.trimOffspring"),sQuery(id+"F0.wireOp",EDGE,"E350.trimOffspring"),sQuery(id+"F0.wireOp",EDGE,"E351.trimOffspring"),sQuery(id+"F0.wireOp",EDGE,"E352.trimOffspring"),sQuery(id+"F0.wireOp",EDGE,"E353.trimOffspring"),sQuery(id+"F0.wireOp",EDGE,"E354.trimOffspring"),sQuery(id+"F0.wireOp",EDGE,"E355.trimOffspring"),sQuery(id+"F0.wireOp",EDGE,"E356.trimOffspring"),sQuery(id+"F0.wireOp",EDGE,"E357.trimOffspring"),sQuery(id+"F0.wireOp",EDGE,"E358.trimOffspring"),sQuery(id+"F0.wireOp",EDGE,"E359.trimOffspring"),sQuery(id+"F0.wireOp",EDGE,"E360.trimOffspring"),sQuery(id+"F0.wireOp",EDGE,"E361.trimOffspring"),sQuery(id+"F0.wireOp",EDGE,"E362.trimOffspring"),sQuery(id+"F0.wireOp",EDGE,"E363.trimOffspring"),sQuery(id+"F0.wireOp",EDGE,"E364.trimOffspring"),sQuery(id+"F0.wireOp",EDGE,"E365.trimOffspring"),sQuery(id+"F0.wireOp",EDGE,"E366.trimOffspring"),sQuery(id+"F0.wireOp",EDGE,"E367.trimOffspring"),sQuery(id+"F0.wireOp",EDGE,"E368.trimOffspring"),sQuery(id+"F0.wireOp",EDGE,"E369.trimOffspring"),sQuery(id+"F0.wireOp",EDGE,"E370.trimOffspring"),sQuery(id+"F0.wireOp",EDGE,"E371.trimOffspring"),sQuery(id+"F0.wireOp",EDGE,"E372.trimOffspring"),sQuery(id+"F0.wireOp",EDGE,"E373.trimOffspring"),sQuery(id+"F0.wireOp",EDGE,"E374.trimOffspring"),sQuery(id+"F0.wireOp",EDGE,"E375.trimOffspring"),sQuery(id+"F0.wireOp",EDGE,"E376.trimOffspring"),sQuery(id+"F0.wireOp",EDGE,"E377.trimOffspring"),sQuery(id+"F0.wireOp",EDGE,"E378.trimOffspring"),sQuery(id+"F0.wireOp",EDGE,"E379.trimOffspring"),sQuery(id+"F0.wireOp",EDGE,"E380.trimOffspring"),sQuery(id+"F0.wireOp",EDGE,"E381.trimOffspring"),sQuery(id+"F0.wireOp",EDGE,"E382.trimOffspring"),sQuery(id+"F0.wireOp",EDGE,"E383.trimOffspring"),sQuery(id+"F0.wireOp",EDGE,"E384.trimOffspring"),sQuery(id+"F0.wireOp",EDGE,"E385.trimOffspring"),sQuery(id+"F0.wireOp",EDGE,"E386.trimOffspring"),sQuery(id+"F0.wireOp",EDGE,"E387.trimOffspring"),sQuery(id+"F0.wireOp",EDGE,"E388.trimOffspring"),sQuery(id+"F0.wireOp",EDGE,"E389.trimOffspring"),sQuery(id+"F0.wireOp",EDGE,"E390.trimOffspring"),sQuery(id+"F0.wireOp",EDGE,"E391.trimOffspring"),sQuery(id+"F0.wireOp",EDGE,"E392.trimOffspring"),sQuery(id+"F0.wireOp",EDGE,"E393.trimOffspring"),sQuery(id+"F0.wireOp",EDGE,"E394.trimOffspring"),sQuery(id+"F0.wireOp",EDGE,"E395.trimOffspring"),sQuery(id+"F0.wireOp",EDGE,"E396.trimOffspring"),sQuery(id+"F0.wireOp",EDGE,"E397.trimOffspring"),sQuery(id+"F0.wireOp",EDGE,"E398.trimOffspring"),sQuery(id+"F0.wireOp",EDGE,"E399.trimOffspring"),sQuery(id+"F0.wireOp",EDGE,"E400.trimOffspring"),sQuery(id+"F0.wireOp",EDGE,"E401.trimOffspring"),sQuery(id+"F0.wireOp",EDGE,"E402.trimOffspring"),sQuery(id+"F0.wireOp",EDGE,"E403.trimOffspring"),sQuery(id+"F0.wireOp",EDGE,"E404.trimOffspring"),sQuery(id+"F0.wireOp",EDGE,"E405.trimOffspring"),sQuery(id+"F0.wireOp",EDGE,"E406.trimOffspring"),sQuery(id+"F0.wireOp",EDGE,"E407.trimOffspring"),sQuery(id+"F0.wireOp",EDGE,"E408.trimOffspring"),sQuery(id+"F0.wireOp",EDGE,"E409.trimOffspring"),sQuery(id+"F0.wireOp",EDGE,"E410.trimOffspring"),sQuery(id+"F0.wireOp",EDGE,"E411.trimOffspring"),sQuery(id+"F0.wireOp",EDGE,"E412.trimOffspring"),sQuery(id+"F0.wireOp",EDGE,"E413.trimOffspring"),sQuery(id+"F0.wireOp",EDGE,"E414.trimOffspring"),sQuery(id+"F0.wireOp",EDGE,"E415.trimOffspring"),sQuery(id+"F0.wireOp",EDGE,"E416.trimOffspring"),sQuery(id+"F0.wireOp",EDGE,"E417.trimOffspring"),sQuery(id+"F0.wireOp",EDGE,"E418.trimOffspring"),sQuery(id+"F0.wireOp",EDGE,"E419.trimOffspring"),sQuery(id+"F0.wireOp",EDGE,"E420.trimOffspring"),sQuery(id+"F0.wireOp",EDGE,"E421.trimOffspring"),sQuery(id+"F0.wireOp",EDGE,"E422.trimOffspring"),sQuery(id+"F0.wireOp",EDGE,"E423.trimOffspring"),sQuery(id+"F0.wireOp",EDGE,"E424.trimOffspring"),sQuery(id+"F0.wireOp",EDGE,"E425.trimOffspring"),sQuery(id+"F0.wireOp",EDGE,"E426.trimOffspring"),sQuery(id+"F0.wireOp",EDGE,"E427.trimOffspring"),sQuery(id+"F0.wireOp",EDGE,"E428.trimOffspring"),sQuery(id+"F0.wireOp",EDGE,"E429.trimOffspring"),sQuery(id+"F0.wireOp",EDGE,"E430.trimOffspring"),sQuery(id+"F0.wireOp",EDGE,"E431.trimOffspring"),sQuery(id+"F0.wireOp",EDGE,"E432.trimOffspring"),sQuery(id+"F0.wireOp",EDGE,"E433.trimOffspring"),sQuery(id+"F0.wireOp",EDGE,"E434.trimOffspring"),sQuery(id+"F0.wireOp",EDGE,"E435.trimOffspring"),sQuery(id+"F0.wireOp",EDGE,"E436.trimOffspring"),sQuery(id+"F0.wireOp",EDGE,"E437.trimOffspring"),sQuery(id+"F0.wireOp",EDGE,"E438.trimOffspring"),sQuery(id+"F0.wireOp",EDGE,"E439.trimOffspring"),sQuery(id+"F0.wireOp",EDGE,"E440.trimOffspring"),sQuery(id+"F0.wireOp",EDGE,"E441.trimOffspring"),sQuery(id+"F0.wireOp",EDGE,"E442.trimOffspring"),sQuery(id+"F0.wireOp",EDGE,"E443.trimOffspring"),sQuery(id+"F0.wireOp",EDGE,"E444.trimOffspring"),sQuery(id+"F0.wireOp",EDGE,"E445.trimOffspring"),sQuery(id+"F0.wireOp",EDGE,"E446.trimOffspring"),sQuery(id+"F0.wireOp",EDGE,"E447.trimOffspring"),sQuery(id+"F0.wireOp",EDGE,"E448.trimOffspring"),sQuery(id+"F0.wireOp",EDGE,"E449.trimOffspring"),sQuery(id+"F0.wireOp",EDGE,"E450.trimOffspring"),sQuery(id+"F0.wireOp",EDGE,"E451.trimOffspring"),sQuery(id+"F0.wireOp",EDGE,"E452.trimOffspring"),sQuery(id+"F0.wireOp",EDGE,"E453.trimOffspring"),sQuery(id+"F0.wireOp",EDGE,"E454.trimOffspring"),sQuery(id+"F0.wireOp",EDGE,"E455.trimOffspring"),sQuery(id+"F0.wireOp",EDGE,"E456.trimOffspring"),sQuery(id+"F0.wireOp",EDGE,"E457.trimOffspring"),sQuery(id+"F0.wireOp",EDGE,"E458.trimOffspring"),sQuery(id+"F0.wireOp",EDGE,"E459.trimOffspring"),sQuery(id+"F0.wireOp",EDGE,"E460.trimOffspring"),sQuery(id+"F0.wireOp",EDGE,"E461.trimOffspring"),sQuery(id+"F0.wireOp",EDGE,"E462.trimOffspring"),sQuery(id+"F0.wireOp",EDGE,"E463.trimOffspring"),sQuery(id+"F0.wireOp",EDGE,"E464.trimOffspring"),sQuery(id+"F0.wireOp",EDGE,"E465.trimOffspring"),sQuery(id+"F0.wireOp",EDGE,"E466.trimOffspring"),sQuery(id+"F0.wireOp",EDGE,"E467.trimOffspring"),sQuery(id+"F0.wireOp",EDGE,"E468"),sQuery(id+"F0.wireOp",EDGE,"E469"),sQuery(id+"F0.wireOp",EDGE,"E470"),sQuery(id+"F0.wireOp",EDGE,"E471")])],"isStart":false});
            var Q1;
            Q1=makeQuery(id+"F0.imprint","IMPRINT",FACE,{"disambiguationData":[TD([[makeQuery(id+"F0.imprint","IMPRINT",EDGE,{"derivedFrom":sQuery(id+"F0.wireOp",EDGE,"E5.2.0")}),-1.0]])]});
            var Q2;
            {var subQ6=sQuery(id+"F0.wireOp",EDGE,"E4.3.0");Q2=makeQuery(id+"F0.imprint","IMPRINT",FACE,{"disambiguationData":[TD([[makeQuery(id+"F0.imprint","IMPRINT",EDGE,{"derivedFrom":subQ6}),1.0]])]});}
            extrude(context, id + "F2", {"entities" : qUnion([Q0, Q1, Q2]), "operationType" : NewBodyOperationType.ADD, "oppositeDirection" : true, "depth" : 1 * mm, "offsetDistance" : 25 * mm});
        }
        {
            var Q0;
            Q0=makeQuery(id+"F0.imprint","IMPRINT",FACE,{"disambiguationData":[TD([[makeQuery(id+"F0.imprint","IMPRINT",EDGE,{"derivedFrom":sQuery(id+"F0.wireOp",EDGE,"E468")}),1.0]])]});
            var Q1;
            Q1=makeQuery(id+"F0.imprint","IMPRINT",FACE,{"disambiguationData":[TD([[makeQuery(id+"F0.imprint","IMPRINT",EDGE,{"derivedFrom":sQuery(id+"F0.wireOp",EDGE,"E469")}),1.0]])]});
            extrude(context, id + "F3", {"entities" : qUnion([Q0, Q1]), "operationType" : NewBodyOperationType.ADD, "oppositeDirection" : true, "depth" : 3.5 * mm, "offsetDistance" : 25 * mm, "hasSecondDirection" : true, "secondDirectionOppositeDirection" : false, "secondDirectionDepth" : 1 * mm});
        }
        {
            var Q0;
            Q0=makeQuery(id+"F0.imprint","IMPRINT",FACE,{"disambiguationData":[TD([[makeQuery(id+"F0.imprint","IMPRINT",EDGE,{"derivedFrom":sQuery(id+"F0.wireOp",EDGE,"E473.converted")}),1.0]])]});
            var Q1;
            Q1=makeQuery(id+"F0.imprint","IMPRINT",FACE,{"disambiguationData":[TD([[makeQuery(id+"F0.imprint","IMPRINT",EDGE,{"derivedFrom":sQuery(id+"F0.wireOp",EDGE,"E472.converted")}),1.0]])]});
            extrude(context, id + "F4", {"entities" : qUnion([Q0, Q1]), "operationType" : NewBodyOperationType.ADD, "oppositeDirection" : true, "depth" : 5.5 * mm, "offsetDistance" : 25 * mm, "hasSecondDirection" : true, "secondDirectionOppositeDirection" : false, "secondDirectionDepth" : 1 * mm});
        }
        {
            var Q0;
            Q0=makeQuery(id+"F4.opExtrude","CAP_EDGE",EDGE,{"disambiguationData":[OSD([sQuery(id+"F0.wireOp",EDGE,"E473.converted")])],"isStart":false});
            var Q1;
            Q1=makeQuery(id+"F4.opExtrude","CAP_EDGE",EDGE,{"disambiguationData":[OSD([sQuery(id+"F0.wireOp",EDGE,"E472.converted")])],"isStart":false});
            chamfer(context, id + "F5", {"entities" : qUnion([Q0, Q1]), "chamferType" : ChamferType.TWO_OFFSETS, "width1" : 2 * mm, "oppositeDirection" : false, "width2" : 0.5 * mm, "tangentPropagation" : true});
        }
        {
            var Q0;
            Q0=makeQuery(id+"F1.opExtrude","SWEPT_EDGE",EDGE,{"disambiguationData":[OSD([sQuery(id+"F0.wireOp",EDGE,"E0"),sQuery(id+"F0.wireOp",EDGE,"E8.trimOffspring")])]});
            var Q1;
            Q1=makeQuery(id+"F1.opExtrude","SWEPT_EDGE",EDGE,{"disambiguationData":[OSD([sQuery(id+"F0.wireOp",EDGE,"E3"),sQuery(id+"F0.wireOp",EDGE,"E14.trimOffspring")])]});
            var Q2;
            Q2=makeQuery(id+"F1.opExtrude","SWEPT_EDGE",EDGE,{"disambiguationData":[OSD([sQuery(id+"F0.wireOp",EDGE,"E8.trimOffspring"),sQuery(id+"F0.wireOp",EDGE,"E14.trimOffspring")])]});
            var Q3;
            Q3=makeQuery(id+"F2.opExtrude","SWEPT_EDGE",EDGE,{"disambiguationData":[OSD([sQuery(id+"F0.wireOp",EDGE,"E0"),sQuery(id+"F0.wireOp",EDGE,"E9.trimOffspring")])]});
            var Q4;
            Q4=makeQuery(id+"F2.opExtrude","SWEPT_EDGE",EDGE,{"disambiguationData":[OSD([sQuery(id+"F0.wireOp",EDGE,"E9.trimOffspring"),sQuery(id+"F0.wireOp",EDGE,"E43.trimOffspring")])]});
            var Q5;
            Q5=makeQuery(id+"F2.opExtrude","SWEPT_EDGE",EDGE,{"disambiguationData":[OSD([sQuery(id+"F0.wireOp",EDGE,"E4.3.0"),sQuery(id+"F0.wireOp",EDGE,"E38.trimOffspring")])]});
            var Q6;
            Q6=makeQuery(id+"F2.opExtrude","SWEPT_EDGE",EDGE,{"disambiguationData":[OSD([sQuery(id+"F0.wireOp",EDGE,"E4.3.0"),sQuery(id+"F0.wireOp",EDGE,"E43.trimOffspring")])]});
            var Q7;
            Q7=makeQuery(id+"F1.opExtrude","SWEPT_EDGE",EDGE,{"disambiguationData":[OSD([sQuery(id+"F0.wireOp",EDGE,"E3"),sQuery(id+"F0.wireOp",EDGE,"E38.trimOffspring")])]});
            fillet(context, id + "F6", {"entities" : qUnion([Q0, Q1, Q2, Q3, Q4, Q5, Q6, Q7]), "radius" : 3.5 * mm, "tangentPropagation" : true, "allowEdgeOverflow" : false});
        }
    });
